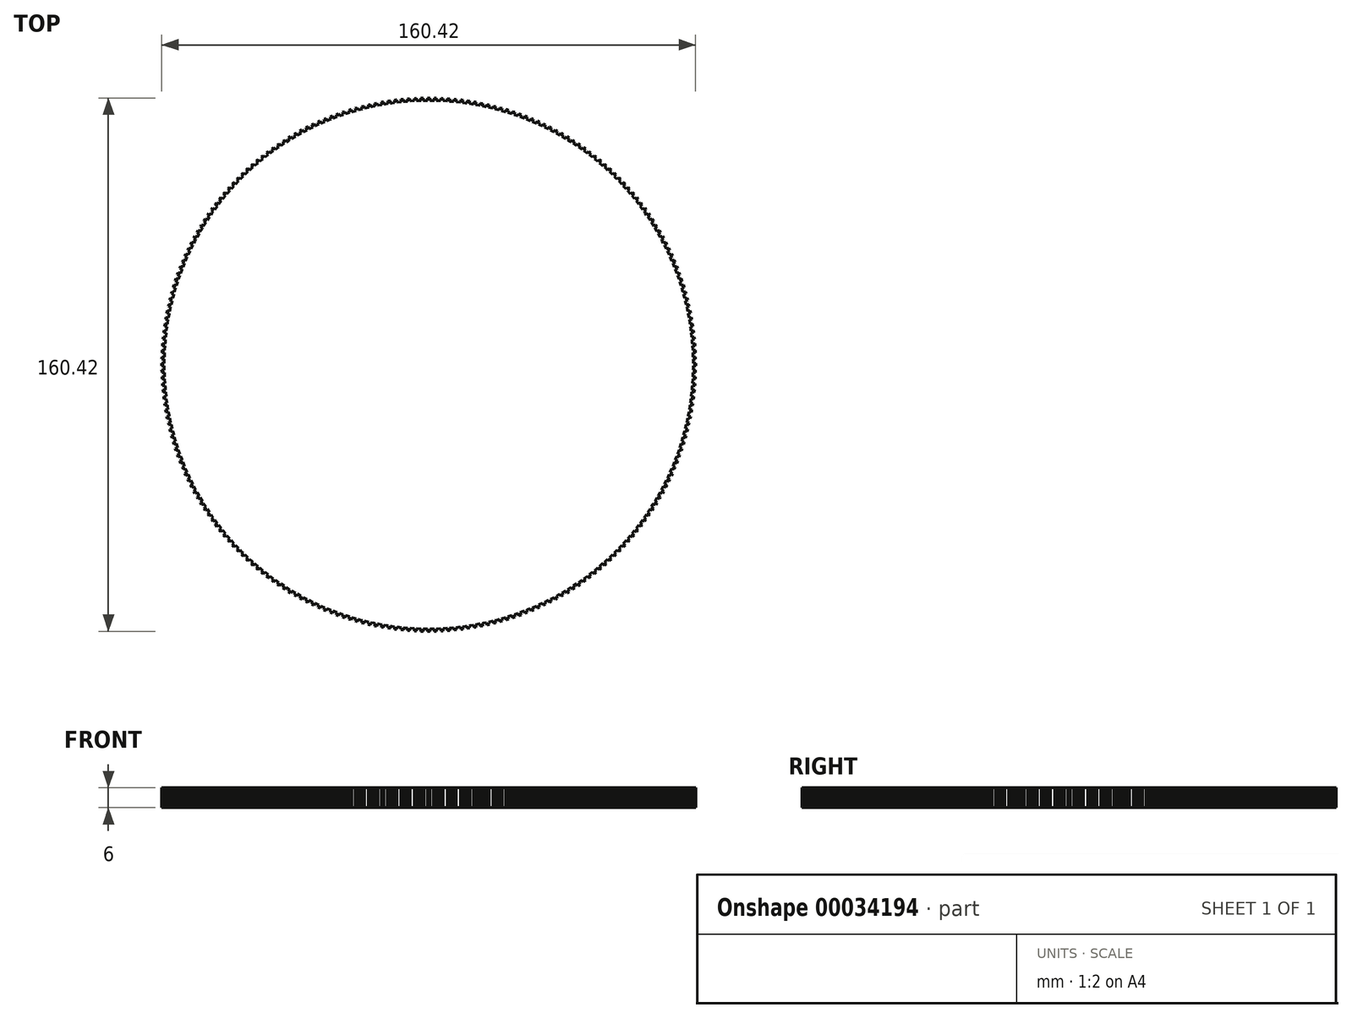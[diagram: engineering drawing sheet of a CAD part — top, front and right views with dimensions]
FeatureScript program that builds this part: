
annotation { "Feature Type Name" : "Feature", "Feature Type Description" : "" }
export const myFeature = defineFeature(function(context is Context, id is Id, definition is map)
    precondition{}
    {
        {
            var Q0;
            Q0=qCreatedBy(makeId("Top.planeOp"),FACE);
            var sketch = newSketch(context, id + "F0", { "sketchPlane" : qUnion([Q0])});
            skLineSegment(sketch, "E0", {"start": v(0.35, -80.21) * mm, "end": v(0.35, -79.46) * mm});
            skLineSegment(sketch, "E1", {"start": v(0.35, -79.46) * mm, "end": v(1.39, -79.45) * mm});
            skLineSegment(sketch, "E2", {"start": v(1.39, -79.45) * mm, "end": v(1.63, -79.45) * mm});
            skLineSegment(sketch, "E3", {"start": v(1.63, -79.45) * mm, "end": v(1.65, -80.2) * mm});
            skLineSegment(sketch, "E4", {"start": v(1.65, -80.2) * mm, "end": v(2.35, -80.18) * mm});
            skLineSegment(sketch, "E5", {"start": v(2.35, -80.18) * mm, "end": v(2.33, -79.43) * mm});
            skLineSegment(sketch, "E6", {"start": v(2.33, -79.43) * mm, "end": v(2.77, -79.42) * mm});
            skLineSegment(sketch, "E7", {"start": v(2.77, -79.42) * mm, "end": v(3.61, -79.38) * mm});
            skLineSegment(sketch, "E8", {"start": v(3.61, -79.38) * mm, "end": v(3.65, -80.13) * mm});
            skLineSegment(sketch, "E9", {"start": v(3.65, -80.13) * mm, "end": v(4.2, -80.1) * mm});
            skLineSegment(sketch, "E10", {"start": v(4.2, -80.1) * mm, "end": v(4.35, -80.1) * mm});
            skLineSegment(sketch, "E11", {"start": v(4.35, -80.1) * mm, "end": v(4.31, -79.35) * mm});
            skLineSegment(sketch, "E12", {"start": v(4.31, -79.35) * mm, "end": v(5.59, -79.27) * mm});
            skLineSegment(sketch, "E13", {"start": v(5.59, -79.27) * mm, "end": v(5.65, -80.01) * mm});
            skLineSegment(sketch, "E14", {"start": v(5.65, -80.01) * mm, "end": v(6.34, -79.96) * mm});
            skLineSegment(sketch, "E15", {"start": v(6.34, -79.96) * mm, "end": v(6.29, -79.21) * mm});
            skLineSegment(sketch, "E16", {"start": v(6.29, -79.21) * mm, "end": v(6.93, -79.16) * mm});
            skLineSegment(sketch, "E17", {"start": v(6.93, -79.16) * mm, "end": v(7.56, -79.1) * mm});
            skLineSegment(sketch, "E18", {"start": v(7.56, -79.1) * mm, "end": v(7.64, -79.85) * mm});
            skLineSegment(sketch, "E19", {"start": v(7.64, -79.85) * mm, "end": v(8.33, -79.78) * mm});
            skLineSegment(sketch, "E20", {"start": v(8.33, -79.78) * mm, "end": v(8.26, -79.03) * mm});
            skLineSegment(sketch, "E21", {"start": v(8.26, -79.03) * mm, "end": v(9.53, -78.89) * mm});
            skLineSegment(sketch, "E22", {"start": v(9.53, -78.89) * mm, "end": v(9.63, -79.63) * mm});
            skLineSegment(sketch, "E23", {"start": v(9.63, -79.63) * mm, "end": v(9.78, -79.62) * mm});
            skLineSegment(sketch, "E24", {"start": v(9.78, -79.62) * mm, "end": v(10.32, -79.54) * mm});
            skLineSegment(sketch, "E25", {"start": v(10.32, -79.54) * mm, "end": v(10.23, -78.8) * mm});
            skLineSegment(sketch, "E26", {"start": v(10.23, -78.8) * mm, "end": v(11.06, -78.7) * mm});
            skLineSegment(sketch, "E27", {"start": v(11.06, -78.7) * mm, "end": v(11.5, -78.63) * mm});
            skLineSegment(sketch, "E28", {"start": v(11.5, -78.63) * mm, "end": v(11.6, -79.37) * mm});
            skLineSegment(sketch, "E29", {"start": v(11.6, -79.37) * mm, "end": v(12.3, -79.26) * mm});
            skLineSegment(sketch, "E30", {"start": v(12.3, -79.26) * mm, "end": v(12.19, -78.52) * mm});
            skLineSegment(sketch, "E31", {"start": v(12.19, -78.52) * mm, "end": v(12.43, -78.49) * mm});
            skLineSegment(sketch, "E32", {"start": v(12.43, -78.49) * mm, "end": v(13.45, -78.31) * mm});
            skLineSegment(sketch, "E33", {"start": v(13.45, -78.31) * mm, "end": v(13.58, -79.05) * mm});
            skLineSegment(sketch, "E34", {"start": v(13.58, -79.05) * mm, "end": v(13.93, -79) * mm});
            skLineSegment(sketch, "E35", {"start": v(13.93, -79) * mm, "end": v(14.27, -78.93) * mm});
            skLineSegment(sketch, "E36", {"start": v(14.27, -78.93) * mm, "end": v(14.14, -78.2) * mm});
            skLineSegment(sketch, "E37", {"start": v(14.14, -78.2) * mm, "end": v(15.16, -78) * mm});
            skLineSegment(sketch, "E38", {"start": v(15.16, -78) * mm, "end": v(15.4, -77.96) * mm});
            skLineSegment(sketch, "E39", {"start": v(15.4, -77.96) * mm, "end": v(15.55, -78.7) * mm});
            skLineSegment(sketch, "E40", {"start": v(15.55, -78.7) * mm, "end": v(16.24, -78.55) * mm});
            skLineSegment(sketch, "E41", {"start": v(16.24, -78.55) * mm, "end": v(16.09, -77.82) * mm});
            skLineSegment(sketch, "E42", {"start": v(16.09, -77.82) * mm, "end": v(16.52, -77.73) * mm});
            skLineSegment(sketch, "E43", {"start": v(16.52, -77.73) * mm, "end": v(17.34, -77.55) * mm});
            skLineSegment(sketch, "E44", {"start": v(17.34, -77.55) * mm, "end": v(17.5, -78.28) * mm});
            skLineSegment(sketch, "E45", {"start": v(17.5, -78.28) * mm, "end": v(18.04, -78.16) * mm});
            skLineSegment(sketch, "E46", {"start": v(18.04, -78.16) * mm, "end": v(18.2, -78.12) * mm});
            skLineSegment(sketch, "E47", {"start": v(18.2, -78.12) * mm, "end": v(18.02, -77.4) * mm});
            skLineSegment(sketch, "E48", {"start": v(18.02, -77.4) * mm, "end": v(19.27, -77.1) * mm});
            skLineSegment(sketch, "E49", {"start": v(19.27, -77.1) * mm, "end": v(19.45, -77.82) * mm});
            skLineSegment(sketch, "E50", {"start": v(19.45, -77.82) * mm, "end": v(20.13, -77.64) * mm});
            skLineSegment(sketch, "E51", {"start": v(20.13, -77.64) * mm, "end": v(19.95, -76.92) * mm});
            skLineSegment(sketch, "E52", {"start": v(19.95, -76.92) * mm, "end": v(20.57, -76.76) * mm});
            skLineSegment(sketch, "E53", {"start": v(20.57, -76.76) * mm, "end": v(21.18, -76.59) * mm});
            skLineSegment(sketch, "E54", {"start": v(21.18, -76.59) * mm, "end": v(21.39, -77.3) * mm});
            skLineSegment(sketch, "E55", {"start": v(21.39, -77.3) * mm, "end": v(22.06, -77.12) * mm});
            skLineSegment(sketch, "E56", {"start": v(22.06, -77.12) * mm, "end": v(21.86, -76.4) * mm});
            skLineSegment(sketch, "E57", {"start": v(21.86, -76.4) * mm, "end": v(23.09, -76.03) * mm});
            skLineSegment(sketch, "E58", {"start": v(23.09, -76.03) * mm, "end": v(23.3, -76.75) * mm});
            skLineSegment(sketch, "E59", {"start": v(23.3, -76.75) * mm, "end": v(23.45, -76.7) * mm});
            skLineSegment(sketch, "E60", {"start": v(23.45, -76.7) * mm, "end": v(23.98, -76.54) * mm});
            skLineSegment(sketch, "E61", {"start": v(23.98, -76.54) * mm, "end": v(23.76, -75.83) * mm});
            skLineSegment(sketch, "E62", {"start": v(23.76, -75.83) * mm, "end": v(24.56, -75.57) * mm});
            skLineSegment(sketch, "E63", {"start": v(24.56, -75.57) * mm, "end": v(24.98, -75.43) * mm});
            skLineSegment(sketch, "E64", {"start": v(24.98, -75.43) * mm, "end": v(25.21, -76.15) * mm});
            skLineSegment(sketch, "E65", {"start": v(25.21, -76.15) * mm, "end": v(25.88, -75.92) * mm});
            skLineSegment(sketch, "E66", {"start": v(25.88, -75.92) * mm, "end": v(25.64, -75.21) * mm});
            skLineSegment(sketch, "E67", {"start": v(25.64, -75.21) * mm, "end": v(25.87, -75.13) * mm});
            skLineSegment(sketch, "E68", {"start": v(25.87, -75.13) * mm, "end": v(26.85, -74.79) * mm});
            skLineSegment(sketch, "E69", {"start": v(26.85, -74.79) * mm, "end": v(27.1, -75.5) * mm});
            skLineSegment(sketch, "E70", {"start": v(27.1, -75.5) * mm, "end": v(27.43, -75.38) * mm});
            skLineSegment(sketch, "E71", {"start": v(27.43, -75.38) * mm, "end": v(27.76, -75.25) * mm});
            skLineSegment(sketch, "E72", {"start": v(27.76, -75.25) * mm, "end": v(27.5, -74.55) * mm});
            skLineSegment(sketch, "E73", {"start": v(27.5, -74.55) * mm, "end": v(28.48, -74.19) * mm});
            skLineSegment(sketch, "E74", {"start": v(28.48, -74.19) * mm, "end": v(28.7, -74.1) * mm});
            skLineSegment(sketch, "E75", {"start": v(28.7, -74.1) * mm, "end": v(28.98, -74.8) * mm});
            skLineSegment(sketch, "E76", {"start": v(28.98, -74.8) * mm, "end": v(29.63, -74.54) * mm});
            skLineSegment(sketch, "E77", {"start": v(29.63, -74.54) * mm, "end": v(29.36, -73.84) * mm});
            skLineSegment(sketch, "E78", {"start": v(29.36, -73.84) * mm, "end": v(29.77, -73.68) * mm});
            skLineSegment(sketch, "E79", {"start": v(29.77, -73.68) * mm, "end": v(30.54, -73.36) * mm});
            skLineSegment(sketch, "E80", {"start": v(30.54, -73.36) * mm, "end": v(30.83, -74.05) * mm});
            skLineSegment(sketch, "E81", {"start": v(30.83, -74.05) * mm, "end": v(31.34, -73.84) * mm});
            skLineSegment(sketch, "E82", {"start": v(31.34, -73.84) * mm, "end": v(31.48, -73.78) * mm});
            skLineSegment(sketch, "E83", {"start": v(31.48, -73.78) * mm, "end": v(31.19, -73.09) * mm});
            skLineSegment(sketch, "E84", {"start": v(31.19, -73.09) * mm, "end": v(32.36, -72.57) * mm});
            skLineSegment(sketch, "E85", {"start": v(32.36, -72.57) * mm, "end": v(32.67, -73.26) * mm});
            skLineSegment(sketch, "E86", {"start": v(32.67, -73.26) * mm, "end": v(33.3, -72.97) * mm});
            skLineSegment(sketch, "E87", {"start": v(33.3, -72.97) * mm, "end": v(33, -72.28) * mm});
            skLineSegment(sketch, "E88", {"start": v(33, -72.28) * mm, "end": v(33.58, -72.02) * mm});
            skLineSegment(sketch, "E89", {"start": v(33.58, -72.02) * mm, "end": v(34.16, -71.74) * mm});
            skLineSegment(sketch, "E90", {"start": v(34.16, -71.74) * mm, "end": v(34.49, -72.42) * mm});
            skLineSegment(sketch, "E91", {"start": v(34.49, -72.42) * mm, "end": v(35.12, -72.12) * mm});
            skLineSegment(sketch, "E92", {"start": v(35.12, -72.12) * mm, "end": v(34.8, -71.44) * mm});
            skLineSegment(sketch, "E93", {"start": v(34.8, -71.44) * mm, "end": v(35.94, -70.87) * mm});
            skLineSegment(sketch, "E94", {"start": v(35.94, -70.87) * mm, "end": v(36.28, -71.54) * mm});
            skLineSegment(sketch, "E95", {"start": v(36.28, -71.54) * mm, "end": v(36.42, -71.47) * mm});
            skLineSegment(sketch, "E96", {"start": v(36.42, -71.47) * mm, "end": v(36.9, -71.22) * mm});
            skLineSegment(sketch, "E97", {"start": v(36.9, -71.22) * mm, "end": v(36.56, -70.55) * mm});
            skLineSegment(sketch, "E98", {"start": v(36.56, -70.55) * mm, "end": v(37.3, -70.16) * mm});
            skLineSegment(sketch, "E99", {"start": v(37.3, -70.16) * mm, "end": v(37.7, -69.95) * mm});
            skLineSegment(sketch, "E100", {"start": v(37.7, -69.95) * mm, "end": v(38.05, -70.61) * mm});
            skLineSegment(sketch, "E101", {"start": v(38.05, -70.61) * mm, "end": v(38.67, -70.28) * mm});
            skLineSegment(sketch, "E102", {"start": v(38.67, -70.28) * mm, "end": v(38.31, -69.62) * mm});
            skLineSegment(sketch, "E103", {"start": v(38.31, -69.62) * mm, "end": v(38.52, -69.5) * mm});
            skLineSegment(sketch, "E104", {"start": v(38.52, -69.5) * mm, "end": v(39.43, -69) * mm});
            skLineSegment(sketch, "E105", {"start": v(39.43, -69) * mm, "end": v(39.8, -69.64) * mm});
            skLineSegment(sketch, "E106", {"start": v(39.8, -69.64) * mm, "end": v(40.1, -69.47) * mm});
            skLineSegment(sketch, "E107", {"start": v(40.1, -69.47) * mm, "end": v(40.4, -69.29) * mm});
            skLineSegment(sketch, "E108", {"start": v(40.4, -69.29) * mm, "end": v(40.03, -68.64) * mm});
            skLineSegment(sketch, "E109", {"start": v(40.03, -68.64) * mm, "end": v(40.93, -68.11) * mm});
            skLineSegment(sketch, "E110", {"start": v(40.93, -68.11) * mm, "end": v(41.14, -67.99) * mm});
            skLineSegment(sketch, "E111", {"start": v(41.14, -67.99) * mm, "end": v(41.53, -68.63) * mm});
            skLineSegment(sketch, "E112", {"start": v(41.53, -68.63) * mm, "end": v(42.12, -68.26) * mm});
            skLineSegment(sketch, "E113", {"start": v(42.12, -68.26) * mm, "end": v(41.73, -67.62) * mm});
            skLineSegment(sketch, "E114", {"start": v(41.73, -67.62) * mm, "end": v(42.1, -67.39) * mm});
            skLineSegment(sketch, "E115", {"start": v(42.1, -67.39) * mm, "end": v(42.82, -66.94) * mm});
            skLineSegment(sketch, "E116", {"start": v(42.82, -66.94) * mm, "end": v(43.22, -67.57) * mm});
            skLineSegment(sketch, "E117", {"start": v(43.22, -67.57) * mm, "end": v(43.69, -67.27) * mm});
            skLineSegment(sketch, "E118", {"start": v(43.69, -67.27) * mm, "end": v(43.81, -67.2) * mm});
            skLineSegment(sketch, "E119", {"start": v(43.81, -67.2) * mm, "end": v(43.4, -66.56) * mm});
            skLineSegment(sketch, "E120", {"start": v(43.4, -66.56) * mm, "end": v(44.47, -65.85) * mm});
            skLineSegment(sketch, "E121", {"start": v(44.47, -65.85) * mm, "end": v(44.9, -66.47) * mm});
            skLineSegment(sketch, "E122", {"start": v(44.9, -66.47) * mm, "end": v(45.47, -66.08) * mm});
            skLineSegment(sketch, "E123", {"start": v(45.47, -66.08) * mm, "end": v(45.05, -65.46) * mm});
            skLineSegment(sketch, "E124", {"start": v(45.05, -65.46) * mm, "end": v(45.58, -65.1) * mm});
            skLineSegment(sketch, "E125", {"start": v(45.58, -65.1) * mm, "end": v(46.1, -64.72) * mm});
            skLineSegment(sketch, "E126", {"start": v(46.1, -64.72) * mm, "end": v(46.54, -65.33) * mm});
            skLineSegment(sketch, "E127", {"start": v(46.54, -65.33) * mm, "end": v(47.1, -64.92) * mm});
            skLineSegment(sketch, "E128", {"start": v(47.1, -64.92) * mm, "end": v(46.67, -64.31) * mm});
            skLineSegment(sketch, "E129", {"start": v(46.67, -64.31) * mm, "end": v(47.7, -63.55) * mm});
            skLineSegment(sketch, "E130", {"start": v(47.7, -63.55) * mm, "end": v(48.15, -64.15) * mm});
            skLineSegment(sketch, "E131", {"start": v(48.15, -64.15) * mm, "end": v(48.27, -64.06) * mm});
            skLineSegment(sketch, "E132", {"start": v(48.27, -64.06) * mm, "end": v(48.71, -63.73) * mm});
            skLineSegment(sketch, "E133", {"start": v(48.71, -63.73) * mm, "end": v(48.26, -63.13) * mm});
            skLineSegment(sketch, "E134", {"start": v(48.26, -63.13) * mm, "end": v(48.92, -62.62) * mm});
            skLineSegment(sketch, "E135", {"start": v(48.92, -62.62) * mm, "end": v(49.27, -62.34) * mm});
            skLineSegment(sketch, "E136", {"start": v(49.27, -62.34) * mm, "end": v(49.74, -62.93) * mm});
            skLineSegment(sketch, "E137", {"start": v(49.74, -62.93) * mm, "end": v(50.28, -62.5) * mm});
            skLineSegment(sketch, "E138", {"start": v(50.28, -62.5) * mm, "end": v(49.82, -61.9) * mm});
            skLineSegment(sketch, "E139", {"start": v(49.82, -61.9) * mm, "end": v(50, -61.76) * mm});
            skLineSegment(sketch, "E140", {"start": v(50, -61.76) * mm, "end": v(50.8, -61.1) * mm});
            skLineSegment(sketch, "E141", {"start": v(50.8, -61.1) * mm, "end": v(51.3, -61.67) * mm});
            skLineSegment(sketch, "E142", {"start": v(51.3, -61.67) * mm, "end": v(51.56, -61.45) * mm});
            skLineSegment(sketch, "E143", {"start": v(51.56, -61.45) * mm, "end": v(51.83, -61.22) * mm});
            skLineSegment(sketch, "E144", {"start": v(51.83, -61.22) * mm, "end": v(51.34, -60.65) * mm});
            skLineSegment(sketch, "E145", {"start": v(51.34, -60.65) * mm, "end": v(52.13, -59.97) * mm});
            skLineSegment(sketch, "E146", {"start": v(52.13, -59.97) * mm, "end": v(52.32, -59.81) * mm});
            skLineSegment(sketch, "E147", {"start": v(52.32, -59.81) * mm, "end": v(52.81, -60.37) * mm});
            skLineSegment(sketch, "E148", {"start": v(52.81, -60.37) * mm, "end": v(53.34, -59.9) * mm});
            skLineSegment(sketch, "E149", {"start": v(53.34, -59.9) * mm, "end": v(52.84, -59.35) * mm});
            skLineSegment(sketch, "E150", {"start": v(52.84, -59.35) * mm, "end": v(53.17, -59.05) * mm});
            skLineSegment(sketch, "E151", {"start": v(53.17, -59.05) * mm, "end": v(53.8, -58.49) * mm});
            skLineSegment(sketch, "E152", {"start": v(53.8, -58.49) * mm, "end": v(54.3, -59.04) * mm});
            skLineSegment(sketch, "E153", {"start": v(54.3, -59.04) * mm, "end": v(54.7, -58.66) * mm});
            skLineSegment(sketch, "E154", {"start": v(54.7, -58.66) * mm, "end": v(54.81, -58.56) * mm});
            skLineSegment(sketch, "E155", {"start": v(54.81, -58.56) * mm, "end": v(54.3, -58.01) * mm});
            skLineSegment(sketch, "E156", {"start": v(54.3, -58.01) * mm, "end": v(55.23, -57.13) * mm});
            skLineSegment(sketch, "E157", {"start": v(55.23, -57.13) * mm, "end": v(55.76, -57.67) * mm});
            skLineSegment(sketch, "E158", {"start": v(55.76, -57.67) * mm, "end": v(56.26, -57.18) * mm});
            skLineSegment(sketch, "E159", {"start": v(56.26, -57.18) * mm, "end": v(55.73, -56.64) * mm});
            skLineSegment(sketch, "E160", {"start": v(55.73, -56.64) * mm, "end": v(56.19, -56.19) * mm});
            skLineSegment(sketch, "E161", {"start": v(56.19, -56.19) * mm, "end": v(56.64, -55.73) * mm});
            skLineSegment(sketch, "E162", {"start": v(56.64, -55.73) * mm, "end": v(57.18, -56.26) * mm});
            skLineSegment(sketch, "E163", {"start": v(57.18, -56.26) * mm, "end": v(57.67, -55.76) * mm});
            skLineSegment(sketch, "E164", {"start": v(57.67, -55.76) * mm, "end": v(57.13, -55.23) * mm});
            skLineSegment(sketch, "E165", {"start": v(57.13, -55.23) * mm, "end": v(58.01, -54.3) * mm});
            skLineSegment(sketch, "E166", {"start": v(58.01, -54.3) * mm, "end": v(58.56, -54.81) * mm});
            skLineSegment(sketch, "E167", {"start": v(58.56, -54.81) * mm, "end": v(58.66, -54.7) * mm});
            skLineSegment(sketch, "E168", {"start": v(58.66, -54.7) * mm, "end": v(59.04, -54.3) * mm});
            skLineSegment(sketch, "E169", {"start": v(59.04, -54.3) * mm, "end": v(58.49, -53.8) * mm});
            skLineSegment(sketch, "E170", {"start": v(58.49, -53.8) * mm, "end": v(59.05, -53.17) * mm});
            skLineSegment(sketch, "E171", {"start": v(59.05, -53.17) * mm, "end": v(59.35, -52.84) * mm});
            skLineSegment(sketch, "E172", {"start": v(59.35, -52.84) * mm, "end": v(59.9, -53.34) * mm});
            skLineSegment(sketch, "E173", {"start": v(59.9, -53.34) * mm, "end": v(60.37, -52.81) * mm});
            skLineSegment(sketch, "E174", {"start": v(60.37, -52.81) * mm, "end": v(59.81, -52.32) * mm});
            skLineSegment(sketch, "E175", {"start": v(59.81, -52.32) * mm, "end": v(59.97, -52.13) * mm});
            skLineSegment(sketch, "E176", {"start": v(59.97, -52.13) * mm, "end": v(60.65, -51.34) * mm});
            skLineSegment(sketch, "E177", {"start": v(60.65, -51.34) * mm, "end": v(61.22, -51.83) * mm});
            skLineSegment(sketch, "E178", {"start": v(61.22, -51.83) * mm, "end": v(61.45, -51.56) * mm});
            skLineSegment(sketch, "E179", {"start": v(61.45, -51.56) * mm, "end": v(61.67, -51.3) * mm});
            skLineSegment(sketch, "E180", {"start": v(61.67, -51.3) * mm, "end": v(61.1, -50.8) * mm});
            skLineSegment(sketch, "E181", {"start": v(61.1, -50.8) * mm, "end": v(61.76, -50) * mm});
            skLineSegment(sketch, "E182", {"start": v(61.76, -50) * mm, "end": v(61.9, -49.82) * mm});
            skLineSegment(sketch, "E183", {"start": v(61.9, -49.82) * mm, "end": v(62.5, -50.28) * mm});
            skLineSegment(sketch, "E184", {"start": v(62.5, -50.28) * mm, "end": v(62.93, -49.74) * mm});
            skLineSegment(sketch, "E185", {"start": v(62.93, -49.74) * mm, "end": v(62.34, -49.27) * mm});
            skLineSegment(sketch, "E186", {"start": v(62.34, -49.27) * mm, "end": v(62.62, -48.92) * mm});
            skLineSegment(sketch, "E187", {"start": v(62.62, -48.92) * mm, "end": v(63.13, -48.26) * mm});
            skLineSegment(sketch, "E188", {"start": v(63.13, -48.26) * mm, "end": v(63.73, -48.71) * mm});
            skLineSegment(sketch, "E189", {"start": v(63.73, -48.71) * mm, "end": v(64.06, -48.27) * mm});
            skLineSegment(sketch, "E190", {"start": v(64.06, -48.27) * mm, "end": v(64.15, -48.15) * mm});
            skLineSegment(sketch, "E191", {"start": v(64.15, -48.15) * mm, "end": v(63.55, -47.7) * mm});
            skLineSegment(sketch, "E192", {"start": v(63.55, -47.7) * mm, "end": v(64.31, -46.67) * mm});
            skLineSegment(sketch, "E193", {"start": v(64.31, -46.67) * mm, "end": v(64.92, -47.1) * mm});
            skLineSegment(sketch, "E194", {"start": v(64.92, -47.1) * mm, "end": v(65.33, -46.54) * mm});
            skLineSegment(sketch, "E195", {"start": v(65.33, -46.54) * mm, "end": v(64.72, -46.1) * mm});
            skLineSegment(sketch, "E196", {"start": v(64.72, -46.1) * mm, "end": v(65.1, -45.58) * mm});
            skLineSegment(sketch, "E197", {"start": v(65.1, -45.58) * mm, "end": v(65.46, -45.05) * mm});
            skLineSegment(sketch, "E198", {"start": v(65.46, -45.05) * mm, "end": v(66.08, -45.47) * mm});
            skLineSegment(sketch, "E199", {"start": v(66.08, -45.47) * mm, "end": v(66.47, -44.9) * mm});
            skLineSegment(sketch, "E200", {"start": v(66.47, -44.9) * mm, "end": v(65.85, -44.47) * mm});
            skLineSegment(sketch, "E201", {"start": v(65.85, -44.47) * mm, "end": v(66.56, -43.4) * mm});
            skLineSegment(sketch, "E202", {"start": v(66.56, -43.4) * mm, "end": v(67.2, -43.81) * mm});
            skLineSegment(sketch, "E203", {"start": v(67.2, -43.81) * mm, "end": v(67.27, -43.69) * mm});
            skLineSegment(sketch, "E204", {"start": v(67.27, -43.69) * mm, "end": v(67.57, -43.22) * mm});
            skLineSegment(sketch, "E205", {"start": v(67.57, -43.22) * mm, "end": v(66.94, -42.82) * mm});
            skLineSegment(sketch, "E206", {"start": v(66.94, -42.82) * mm, "end": v(67.39, -42.1) * mm});
            skLineSegment(sketch, "E207", {"start": v(67.39, -42.1) * mm, "end": v(67.62, -41.73) * mm});
            skLineSegment(sketch, "E208", {"start": v(67.62, -41.73) * mm, "end": v(68.26, -42.12) * mm});
            skLineSegment(sketch, "E209", {"start": v(68.26, -42.12) * mm, "end": v(68.63, -41.53) * mm});
            skLineSegment(sketch, "E210", {"start": v(68.63, -41.53) * mm, "end": v(67.99, -41.14) * mm});
            skLineSegment(sketch, "E211", {"start": v(67.99, -41.14) * mm, "end": v(68.11, -40.93) * mm});
            skLineSegment(sketch, "E212", {"start": v(68.11, -40.93) * mm, "end": v(68.64, -40.03) * mm});
            skLineSegment(sketch, "E213", {"start": v(68.64, -40.03) * mm, "end": v(69.29, -40.4) * mm});
            skLineSegment(sketch, "E214", {"start": v(69.29, -40.4) * mm, "end": v(69.47, -40.1) * mm});
            skLineSegment(sketch, "E215", {"start": v(69.47, -40.1) * mm, "end": v(69.64, -39.8) * mm});
            skLineSegment(sketch, "E216", {"start": v(69.64, -39.8) * mm, "end": v(69, -39.43) * mm});
            skLineSegment(sketch, "E217", {"start": v(69, -39.43) * mm, "end": v(69.5, -38.52) * mm});
            skLineSegment(sketch, "E218", {"start": v(69.5, -38.52) * mm, "end": v(69.62, -38.31) * mm});
            skLineSegment(sketch, "E219", {"start": v(69.62, -38.31) * mm, "end": v(70.28, -38.67) * mm});
            skLineSegment(sketch, "E220", {"start": v(70.28, -38.67) * mm, "end": v(70.61, -38.05) * mm});
            skLineSegment(sketch, "E221", {"start": v(70.61, -38.05) * mm, "end": v(69.95, -37.7) * mm});
            skLineSegment(sketch, "E222", {"start": v(69.95, -37.7) * mm, "end": v(70.16, -37.3) * mm});
            skLineSegment(sketch, "E223", {"start": v(70.16, -37.3) * mm, "end": v(70.55, -36.56) * mm});
            skLineSegment(sketch, "E224", {"start": v(70.55, -36.56) * mm, "end": v(71.22, -36.9) * mm});
            skLineSegment(sketch, "E225", {"start": v(71.22, -36.9) * mm, "end": v(71.47, -36.42) * mm});
            skLineSegment(sketch, "E226", {"start": v(71.47, -36.42) * mm, "end": v(71.54, -36.28) * mm});
            skLineSegment(sketch, "E227", {"start": v(71.54, -36.28) * mm, "end": v(70.87, -35.94) * mm});
            skLineSegment(sketch, "E228", {"start": v(70.87, -35.94) * mm, "end": v(71.44, -34.8) * mm});
            skLineSegment(sketch, "E229", {"start": v(71.44, -34.8) * mm, "end": v(72.12, -35.12) * mm});
            skLineSegment(sketch, "E230", {"start": v(72.12, -35.12) * mm, "end": v(72.42, -34.49) * mm});
            skLineSegment(sketch, "E231", {"start": v(72.42, -34.49) * mm, "end": v(71.74, -34.16) * mm});
            skLineSegment(sketch, "E232", {"start": v(71.74, -34.16) * mm, "end": v(72.02, -33.58) * mm});
            skLineSegment(sketch, "E233", {"start": v(72.02, -33.58) * mm, "end": v(72.28, -33) * mm});
            skLineSegment(sketch, "E234", {"start": v(72.28, -33) * mm, "end": v(72.97, -33.3) * mm});
            skLineSegment(sketch, "E235", {"start": v(72.97, -33.3) * mm, "end": v(73.26, -32.67) * mm});
            skLineSegment(sketch, "E236", {"start": v(73.26, -32.67) * mm, "end": v(72.57, -32.36) * mm});
            skLineSegment(sketch, "E237", {"start": v(72.57, -32.36) * mm, "end": v(73.09, -31.19) * mm});
            skLineSegment(sketch, "E238", {"start": v(73.09, -31.19) * mm, "end": v(73.78, -31.48) * mm});
            skLineSegment(sketch, "E239", {"start": v(73.78, -31.48) * mm, "end": v(73.84, -31.34) * mm});
            skLineSegment(sketch, "E240", {"start": v(73.84, -31.34) * mm, "end": v(74.05, -30.83) * mm});
            skLineSegment(sketch, "E241", {"start": v(74.05, -30.83) * mm, "end": v(73.36, -30.54) * mm});
            skLineSegment(sketch, "E242", {"start": v(73.36, -30.54) * mm, "end": v(73.68, -29.77) * mm});
            skLineSegment(sketch, "E243", {"start": v(73.68, -29.77) * mm, "end": v(73.84, -29.36) * mm});
            skLineSegment(sketch, "E244", {"start": v(73.84, -29.36) * mm, "end": v(74.54, -29.63) * mm});
            skLineSegment(sketch, "E245", {"start": v(74.54, -29.63) * mm, "end": v(74.8, -28.98) * mm});
            skLineSegment(sketch, "E246", {"start": v(74.8, -28.98) * mm, "end": v(74.1, -28.7) * mm});
            skLineSegment(sketch, "E247", {"start": v(74.1, -28.7) * mm, "end": v(74.19, -28.48) * mm});
            skLineSegment(sketch, "E248", {"start": v(74.19, -28.48) * mm, "end": v(74.55, -27.5) * mm});
            skLineSegment(sketch, "E249", {"start": v(74.55, -27.5) * mm, "end": v(75.25, -27.76) * mm});
            skLineSegment(sketch, "E250", {"start": v(75.25, -27.76) * mm, "end": v(75.38, -27.43) * mm});
            skLineSegment(sketch, "E251", {"start": v(75.38, -27.43) * mm, "end": v(75.5, -27.1) * mm});
            skLineSegment(sketch, "E252", {"start": v(75.5, -27.1) * mm, "end": v(74.79, -26.85) * mm});
            skLineSegment(sketch, "E253", {"start": v(74.79, -26.85) * mm, "end": v(75.13, -25.87) * mm});
            skLineSegment(sketch, "E254", {"start": v(75.13, -25.87) * mm, "end": v(75.21, -25.64) * mm});
            skLineSegment(sketch, "E255", {"start": v(75.21, -25.64) * mm, "end": v(75.92, -25.88) * mm});
            skLineSegment(sketch, "E256", {"start": v(75.92, -25.88) * mm, "end": v(76.15, -25.21) * mm});
            skLineSegment(sketch, "E257", {"start": v(76.15, -25.21) * mm, "end": v(75.43, -24.98) * mm});
            skLineSegment(sketch, "E258", {"start": v(75.43, -24.98) * mm, "end": v(75.57, -24.56) * mm});
            skLineSegment(sketch, "E259", {"start": v(75.57, -24.56) * mm, "end": v(75.83, -23.76) * mm});
            skLineSegment(sketch, "E260", {"start": v(75.83, -23.76) * mm, "end": v(76.54, -23.98) * mm});
            skLineSegment(sketch, "E261", {"start": v(76.54, -23.98) * mm, "end": v(76.7, -23.45) * mm});
            skLineSegment(sketch, "E262", {"start": v(76.7, -23.45) * mm, "end": v(76.75, -23.3) * mm});
            skLineSegment(sketch, "E263", {"start": v(76.75, -23.3) * mm, "end": v(76.03, -23.09) * mm});
            skLineSegment(sketch, "E264", {"start": v(76.03, -23.09) * mm, "end": v(76.4, -21.86) * mm});
            skLineSegment(sketch, "E265", {"start": v(76.4, -21.86) * mm, "end": v(77.12, -22.06) * mm});
            skLineSegment(sketch, "E266", {"start": v(77.12, -22.06) * mm, "end": v(77.3, -21.39) * mm});
            skLineSegment(sketch, "E267", {"start": v(77.3, -21.39) * mm, "end": v(76.59, -21.18) * mm});
            skLineSegment(sketch, "E268", {"start": v(76.59, -21.18) * mm, "end": v(76.76, -20.57) * mm});
            skLineSegment(sketch, "E269", {"start": v(76.76, -20.57) * mm, "end": v(76.92, -19.95) * mm});
            skLineSegment(sketch, "E270", {"start": v(76.92, -19.95) * mm, "end": v(77.64, -20.13) * mm});
            skLineSegment(sketch, "E271", {"start": v(77.64, -20.13) * mm, "end": v(77.82, -19.45) * mm});
            skLineSegment(sketch, "E272", {"start": v(77.82, -19.45) * mm, "end": v(77.1, -19.27) * mm});
            skLineSegment(sketch, "E273", {"start": v(77.1, -19.27) * mm, "end": v(77.4, -18.02) * mm});
            skLineSegment(sketch, "E274", {"start": v(77.4, -18.02) * mm, "end": v(78.12, -18.2) * mm});
            skLineSegment(sketch, "E275", {"start": v(78.12, -18.2) * mm, "end": v(78.16, -18.04) * mm});
            skLineSegment(sketch, "E276", {"start": v(78.16, -18.04) * mm, "end": v(78.28, -17.5) * mm});
            skLineSegment(sketch, "E277", {"start": v(78.28, -17.5) * mm, "end": v(77.55, -17.34) * mm});
            skLineSegment(sketch, "E278", {"start": v(77.55, -17.34) * mm, "end": v(77.73, -16.52) * mm});
            skLineSegment(sketch, "E279", {"start": v(77.73, -16.52) * mm, "end": v(77.82, -16.09) * mm});
            skLineSegment(sketch, "E280", {"start": v(77.82, -16.09) * mm, "end": v(78.55, -16.24) * mm});
            skLineSegment(sketch, "E281", {"start": v(78.55, -16.24) * mm, "end": v(78.7, -15.55) * mm});
            skLineSegment(sketch, "E282", {"start": v(78.7, -15.55) * mm, "end": v(77.96, -15.4) * mm});
            skLineSegment(sketch, "E283", {"start": v(77.96, -15.4) * mm, "end": v(78, -15.16) * mm});
            skLineSegment(sketch, "E284", {"start": v(78, -15.16) * mm, "end": v(78.2, -14.14) * mm});
            skLineSegment(sketch, "E285", {"start": v(78.2, -14.14) * mm, "end": v(78.93, -14.27) * mm});
            skLineSegment(sketch, "E286", {"start": v(78.93, -14.27) * mm, "end": v(79, -13.93) * mm});
            skLineSegment(sketch, "E287", {"start": v(79, -13.93) * mm, "end": v(79.05, -13.58) * mm});
            skLineSegment(sketch, "E288", {"start": v(79.05, -13.58) * mm, "end": v(78.31, -13.45) * mm});
            skLineSegment(sketch, "E289", {"start": v(78.31, -13.45) * mm, "end": v(78.49, -12.43) * mm});
            skLineSegment(sketch, "E290", {"start": v(78.49, -12.43) * mm, "end": v(78.52, -12.19) * mm});
            skLineSegment(sketch, "E291", {"start": v(78.52, -12.19) * mm, "end": v(79.26, -12.3) * mm});
            skLineSegment(sketch, "E292", {"start": v(79.26, -12.3) * mm, "end": v(79.37, -11.6) * mm});
            skLineSegment(sketch, "E293", {"start": v(79.37, -11.6) * mm, "end": v(78.63, -11.5) * mm});
            skLineSegment(sketch, "E294", {"start": v(78.63, -11.5) * mm, "end": v(78.7, -11.06) * mm});
            skLineSegment(sketch, "E295", {"start": v(78.7, -11.06) * mm, "end": v(78.8, -10.23) * mm});
            skLineSegment(sketch, "E296", {"start": v(78.8, -10.23) * mm, "end": v(79.54, -10.32) * mm});
            skLineSegment(sketch, "E297", {"start": v(79.54, -10.32) * mm, "end": v(79.62, -9.78) * mm});
            skLineSegment(sketch, "E298", {"start": v(79.62, -9.78) * mm, "end": v(79.63, -9.63) * mm});
            skLineSegment(sketch, "E299", {"start": v(79.63, -9.63) * mm, "end": v(78.89, -9.53) * mm});
            skLineSegment(sketch, "E300", {"start": v(78.89, -9.53) * mm, "end": v(79.03, -8.26) * mm});
            skLineSegment(sketch, "E301", {"start": v(79.03, -8.26) * mm, "end": v(79.78, -8.33) * mm});
            skLineSegment(sketch, "E302", {"start": v(79.78, -8.33) * mm, "end": v(79.85, -7.64) * mm});
            skLineSegment(sketch, "E303", {"start": v(79.85, -7.64) * mm, "end": v(79.1, -7.56) * mm});
            skLineSegment(sketch, "E304", {"start": v(79.1, -7.56) * mm, "end": v(79.16, -6.93) * mm});
            skLineSegment(sketch, "E305", {"start": v(79.16, -6.93) * mm, "end": v(79.21, -6.29) * mm});
            skLineSegment(sketch, "E306", {"start": v(79.21, -6.29) * mm, "end": v(79.96, -6.34) * mm});
            skLineSegment(sketch, "E307", {"start": v(79.96, -6.34) * mm, "end": v(80.01, -5.65) * mm});
            skLineSegment(sketch, "E308", {"start": v(80.01, -5.65) * mm, "end": v(79.27, -5.59) * mm});
            skLineSegment(sketch, "E309", {"start": v(79.27, -5.59) * mm, "end": v(79.35, -4.31) * mm});
            skLineSegment(sketch, "E310", {"start": v(79.35, -4.31) * mm, "end": v(80.1, -4.35) * mm});
            skLineSegment(sketch, "E311", {"start": v(80.1, -4.35) * mm, "end": v(80.1, -4.2) * mm});
            skLineSegment(sketch, "E312", {"start": v(80.1, -4.2) * mm, "end": v(80.13, -3.65) * mm});
            skLineSegment(sketch, "E313", {"start": v(80.13, -3.65) * mm, "end": v(79.38, -3.61) * mm});
            skLineSegment(sketch, "E314", {"start": v(79.38, -3.61) * mm, "end": v(79.42, -2.77) * mm});
            skLineSegment(sketch, "E315", {"start": v(79.42, -2.77) * mm, "end": v(79.43, -2.33) * mm});
            skLineSegment(sketch, "E316", {"start": v(79.43, -2.33) * mm, "end": v(80.18, -2.35) * mm});
            skLineSegment(sketch, "E317", {"start": v(80.18, -2.35) * mm, "end": v(80.2, -1.65) * mm});
            skLineSegment(sketch, "E318", {"start": v(80.2, -1.65) * mm, "end": v(79.45, -1.63) * mm});
            skLineSegment(sketch, "E319", {"start": v(79.45, -1.63) * mm, "end": v(79.45, -1.39) * mm});
            skLineSegment(sketch, "E320", {"start": v(79.45, -1.39) * mm, "end": v(79.46, -0.35) * mm});
            skLineSegment(sketch, "E321", {"start": v(79.46, -0.35) * mm, "end": v(80.21, -0.35) * mm});
            skLineSegment(sketch, "E322", {"start": v(80.21, -0.35) * mm, "end": v(80.21, 0) * mm});
            skLineSegment(sketch, "E323", {"start": v(80.21, 0) * mm, "end": v(80.21, 0.35) * mm});
            skLineSegment(sketch, "E324", {"start": v(80.21, 0.35) * mm, "end": v(79.46, 0.35) * mm});
            skLineSegment(sketch, "E325", {"start": v(79.46, 0.35) * mm, "end": v(79.45, 1.39) * mm});
            skLineSegment(sketch, "E326", {"start": v(79.45, 1.39) * mm, "end": v(79.45, 1.63) * mm});
            skLineSegment(sketch, "E327", {"start": v(79.45, 1.63) * mm, "end": v(80.2, 1.65) * mm});
            skLineSegment(sketch, "E328", {"start": v(80.2, 1.65) * mm, "end": v(80.18, 2.35) * mm});
            skLineSegment(sketch, "E329", {"start": v(80.18, 2.35) * mm, "end": v(79.43, 2.33) * mm});
            skLineSegment(sketch, "E330", {"start": v(79.43, 2.33) * mm, "end": v(79.42, 2.77) * mm});
            skLineSegment(sketch, "E331", {"start": v(79.42, 2.77) * mm, "end": v(79.38, 3.61) * mm});
            skLineSegment(sketch, "E332", {"start": v(79.38, 3.61) * mm, "end": v(80.13, 3.65) * mm});
            skLineSegment(sketch, "E333", {"start": v(80.13, 3.65) * mm, "end": v(80.1, 4.2) * mm});
            skLineSegment(sketch, "E334", {"start": v(80.1, 4.2) * mm, "end": v(80.1, 4.35) * mm});
            skLineSegment(sketch, "E335", {"start": v(80.1, 4.35) * mm, "end": v(79.35, 4.31) * mm});
            skLineSegment(sketch, "E336", {"start": v(79.35, 4.31) * mm, "end": v(79.27, 5.59) * mm});
            skLineSegment(sketch, "E337", {"start": v(79.27, 5.59) * mm, "end": v(80.01, 5.65) * mm});
            skLineSegment(sketch, "E338", {"start": v(80.01, 5.65) * mm, "end": v(79.96, 6.34) * mm});
            skLineSegment(sketch, "E339", {"start": v(79.96, 6.34) * mm, "end": v(79.21, 6.29) * mm});
            skLineSegment(sketch, "E340", {"start": v(79.21, 6.29) * mm, "end": v(79.16, 6.93) * mm});
            skLineSegment(sketch, "E341", {"start": v(79.16, 6.93) * mm, "end": v(79.1, 7.56) * mm});
            skLineSegment(sketch, "E342", {"start": v(79.1, 7.56) * mm, "end": v(79.85, 7.64) * mm});
            skLineSegment(sketch, "E343", {"start": v(79.85, 7.64) * mm, "end": v(79.78, 8.33) * mm});
            skLineSegment(sketch, "E344", {"start": v(79.78, 8.33) * mm, "end": v(79.03, 8.26) * mm});
            skLineSegment(sketch, "E345", {"start": v(79.03, 8.26) * mm, "end": v(78.89, 9.53) * mm});
            skLineSegment(sketch, "E346", {"start": v(78.89, 9.53) * mm, "end": v(79.63, 9.63) * mm});
            skLineSegment(sketch, "E347", {"start": v(79.63, 9.63) * mm, "end": v(79.62, 9.78) * mm});
            skLineSegment(sketch, "E348", {"start": v(79.62, 9.78) * mm, "end": v(79.54, 10.32) * mm});
            skLineSegment(sketch, "E349", {"start": v(79.54, 10.32) * mm, "end": v(78.8, 10.23) * mm});
            skLineSegment(sketch, "E350", {"start": v(78.8, 10.23) * mm, "end": v(78.7, 11.06) * mm});
            skLineSegment(sketch, "E351", {"start": v(78.7, 11.06) * mm, "end": v(78.63, 11.5) * mm});
            skLineSegment(sketch, "E352", {"start": v(78.63, 11.5) * mm, "end": v(79.37, 11.6) * mm});
            skLineSegment(sketch, "E353", {"start": v(79.37, 11.6) * mm, "end": v(79.26, 12.3) * mm});
            skLineSegment(sketch, "E354", {"start": v(79.26, 12.3) * mm, "end": v(78.52, 12.19) * mm});
            skLineSegment(sketch, "E355", {"start": v(78.52, 12.19) * mm, "end": v(78.49, 12.43) * mm});
            skLineSegment(sketch, "E356", {"start": v(78.49, 12.43) * mm, "end": v(78.31, 13.45) * mm});
            skLineSegment(sketch, "E357", {"start": v(78.31, 13.45) * mm, "end": v(79.05, 13.58) * mm});
            skLineSegment(sketch, "E358", {"start": v(79.05, 13.58) * mm, "end": v(79, 13.93) * mm});
            skLineSegment(sketch, "E359", {"start": v(79, 13.93) * mm, "end": v(78.93, 14.27) * mm});
            skLineSegment(sketch, "E360", {"start": v(78.93, 14.27) * mm, "end": v(78.2, 14.14) * mm});
            skLineSegment(sketch, "E361", {"start": v(78.2, 14.14) * mm, "end": v(78, 15.16) * mm});
            skLineSegment(sketch, "E362", {"start": v(78, 15.16) * mm, "end": v(77.96, 15.4) * mm});
            skLineSegment(sketch, "E363", {"start": v(77.96, 15.4) * mm, "end": v(78.7, 15.55) * mm});
            skLineSegment(sketch, "E364", {"start": v(78.7, 15.55) * mm, "end": v(78.55, 16.24) * mm});
            skLineSegment(sketch, "E365", {"start": v(78.55, 16.24) * mm, "end": v(77.82, 16.09) * mm});
            skLineSegment(sketch, "E366", {"start": v(77.82, 16.09) * mm, "end": v(77.73, 16.52) * mm});
            skLineSegment(sketch, "E367", {"start": v(77.73, 16.52) * mm, "end": v(77.55, 17.34) * mm});
            skLineSegment(sketch, "E368", {"start": v(77.55, 17.34) * mm, "end": v(78.28, 17.5) * mm});
            skLineSegment(sketch, "E369", {"start": v(78.28, 17.5) * mm, "end": v(78.16, 18.04) * mm});
            skLineSegment(sketch, "E370", {"start": v(78.16, 18.04) * mm, "end": v(78.12, 18.2) * mm});
            skLineSegment(sketch, "E371", {"start": v(78.12, 18.2) * mm, "end": v(77.4, 18.02) * mm});
            skLineSegment(sketch, "E372", {"start": v(77.4, 18.02) * mm, "end": v(77.1, 19.27) * mm});
            skLineSegment(sketch, "E373", {"start": v(77.1, 19.27) * mm, "end": v(77.82, 19.45) * mm});
            skLineSegment(sketch, "E374", {"start": v(77.82, 19.45) * mm, "end": v(77.64, 20.13) * mm});
            skLineSegment(sketch, "E375", {"start": v(77.64, 20.13) * mm, "end": v(76.92, 19.95) * mm});
            skLineSegment(sketch, "E376", {"start": v(76.92, 19.95) * mm, "end": v(76.76, 20.57) * mm});
            skLineSegment(sketch, "E377", {"start": v(76.76, 20.57) * mm, "end": v(76.59, 21.18) * mm});
            skLineSegment(sketch, "E378", {"start": v(76.59, 21.18) * mm, "end": v(77.3, 21.39) * mm});
            skLineSegment(sketch, "E379", {"start": v(77.3, 21.39) * mm, "end": v(77.12, 22.06) * mm});
            skLineSegment(sketch, "E380", {"start": v(77.12, 22.06) * mm, "end": v(76.4, 21.86) * mm});
            skLineSegment(sketch, "E381", {"start": v(76.4, 21.86) * mm, "end": v(76.03, 23.09) * mm});
            skLineSegment(sketch, "E382", {"start": v(76.03, 23.09) * mm, "end": v(76.75, 23.3) * mm});
            skLineSegment(sketch, "E383", {"start": v(76.75, 23.3) * mm, "end": v(76.7, 23.45) * mm});
            skLineSegment(sketch, "E384", {"start": v(76.7, 23.45) * mm, "end": v(76.54, 23.98) * mm});
            skLineSegment(sketch, "E385", {"start": v(76.54, 23.98) * mm, "end": v(75.83, 23.76) * mm});
            skLineSegment(sketch, "E386", {"start": v(75.83, 23.76) * mm, "end": v(75.57, 24.56) * mm});
            skLineSegment(sketch, "E387", {"start": v(75.57, 24.56) * mm, "end": v(75.43, 24.98) * mm});
            skLineSegment(sketch, "E388", {"start": v(75.43, 24.98) * mm, "end": v(76.15, 25.21) * mm});
            skLineSegment(sketch, "E389", {"start": v(76.15, 25.21) * mm, "end": v(75.92, 25.88) * mm});
            skLineSegment(sketch, "E390", {"start": v(75.92, 25.88) * mm, "end": v(75.21, 25.64) * mm});
            skLineSegment(sketch, "E391", {"start": v(75.21, 25.64) * mm, "end": v(75.13, 25.87) * mm});
            skLineSegment(sketch, "E392", {"start": v(75.13, 25.87) * mm, "end": v(74.79, 26.85) * mm});
            skLineSegment(sketch, "E393", {"start": v(74.79, 26.85) * mm, "end": v(75.5, 27.1) * mm});
            skLineSegment(sketch, "E394", {"start": v(75.5, 27.1) * mm, "end": v(75.38, 27.43) * mm});
            skLineSegment(sketch, "E395", {"start": v(75.38, 27.43) * mm, "end": v(75.25, 27.76) * mm});
            skLineSegment(sketch, "E396", {"start": v(75.25, 27.76) * mm, "end": v(74.55, 27.5) * mm});
            skLineSegment(sketch, "E397", {"start": v(74.55, 27.5) * mm, "end": v(74.19, 28.48) * mm});
            skLineSegment(sketch, "E398", {"start": v(74.19, 28.48) * mm, "end": v(74.1, 28.7) * mm});
            skLineSegment(sketch, "E399", {"start": v(74.1, 28.7) * mm, "end": v(74.8, 28.98) * mm});
            skLineSegment(sketch, "E400", {"start": v(74.8, 28.98) * mm, "end": v(74.54, 29.63) * mm});
            skLineSegment(sketch, "E401", {"start": v(74.54, 29.63) * mm, "end": v(73.84, 29.36) * mm});
            skLineSegment(sketch, "E402", {"start": v(73.84, 29.36) * mm, "end": v(73.68, 29.77) * mm});
            skLineSegment(sketch, "E403", {"start": v(73.68, 29.77) * mm, "end": v(73.36, 30.54) * mm});
            skLineSegment(sketch, "E404", {"start": v(73.36, 30.54) * mm, "end": v(74.05, 30.83) * mm});
            skLineSegment(sketch, "E405", {"start": v(74.05, 30.83) * mm, "end": v(73.84, 31.34) * mm});
            skLineSegment(sketch, "E406", {"start": v(73.84, 31.34) * mm, "end": v(73.78, 31.48) * mm});
            skLineSegment(sketch, "E407", {"start": v(73.78, 31.48) * mm, "end": v(73.09, 31.19) * mm});
            skLineSegment(sketch, "E408", {"start": v(73.09, 31.19) * mm, "end": v(72.57, 32.36) * mm});
            skLineSegment(sketch, "E409", {"start": v(72.57, 32.36) * mm, "end": v(73.26, 32.67) * mm});
            skLineSegment(sketch, "E410", {"start": v(73.26, 32.67) * mm, "end": v(72.97, 33.3) * mm});
            skLineSegment(sketch, "E411", {"start": v(72.97, 33.3) * mm, "end": v(72.28, 33) * mm});
            skLineSegment(sketch, "E412", {"start": v(72.28, 33) * mm, "end": v(72.02, 33.58) * mm});
            skLineSegment(sketch, "E413", {"start": v(72.02, 33.58) * mm, "end": v(71.74, 34.16) * mm});
            skLineSegment(sketch, "E414", {"start": v(71.74, 34.16) * mm, "end": v(72.42, 34.49) * mm});
            skLineSegment(sketch, "E415", {"start": v(72.42, 34.49) * mm, "end": v(72.12, 35.12) * mm});
            skLineSegment(sketch, "E416", {"start": v(72.12, 35.12) * mm, "end": v(71.44, 34.8) * mm});
            skLineSegment(sketch, "E417", {"start": v(71.44, 34.8) * mm, "end": v(70.87, 35.94) * mm});
            skLineSegment(sketch, "E418", {"start": v(70.87, 35.94) * mm, "end": v(71.54, 36.28) * mm});
            skLineSegment(sketch, "E419", {"start": v(71.54, 36.28) * mm, "end": v(71.47, 36.42) * mm});
            skLineSegment(sketch, "E420", {"start": v(71.47, 36.42) * mm, "end": v(71.22, 36.9) * mm});
            skLineSegment(sketch, "E421", {"start": v(71.22, 36.9) * mm, "end": v(70.55, 36.56) * mm});
            skLineSegment(sketch, "E422", {"start": v(70.55, 36.56) * mm, "end": v(70.16, 37.3) * mm});
            skLineSegment(sketch, "E423", {"start": v(70.16, 37.3) * mm, "end": v(69.95, 37.7) * mm});
            skLineSegment(sketch, "E424", {"start": v(69.95, 37.7) * mm, "end": v(70.61, 38.05) * mm});
            skLineSegment(sketch, "E425", {"start": v(70.61, 38.05) * mm, "end": v(70.28, 38.67) * mm});
            skLineSegment(sketch, "E426", {"start": v(70.28, 38.67) * mm, "end": v(69.62, 38.31) * mm});
            skLineSegment(sketch, "E427", {"start": v(69.62, 38.31) * mm, "end": v(69.5, 38.52) * mm});
            skLineSegment(sketch, "E428", {"start": v(69.5, 38.52) * mm, "end": v(69, 39.43) * mm});
            skLineSegment(sketch, "E429", {"start": v(69, 39.43) * mm, "end": v(69.64, 39.8) * mm});
            skLineSegment(sketch, "E430", {"start": v(69.64, 39.8) * mm, "end": v(69.47, 40.1) * mm});
            skLineSegment(sketch, "E431", {"start": v(69.47, 40.1) * mm, "end": v(69.29, 40.4) * mm});
            skLineSegment(sketch, "E432", {"start": v(69.29, 40.4) * mm, "end": v(68.64, 40.03) * mm});
            skLineSegment(sketch, "E433", {"start": v(68.64, 40.03) * mm, "end": v(68.11, 40.93) * mm});
            skLineSegment(sketch, "E434", {"start": v(68.11, 40.93) * mm, "end": v(67.99, 41.14) * mm});
            skLineSegment(sketch, "E435", {"start": v(67.99, 41.14) * mm, "end": v(68.63, 41.53) * mm});
            skLineSegment(sketch, "E436", {"start": v(68.63, 41.53) * mm, "end": v(68.26, 42.12) * mm});
            skLineSegment(sketch, "E437", {"start": v(68.26, 42.12) * mm, "end": v(67.62, 41.73) * mm});
            skLineSegment(sketch, "E438", {"start": v(67.62, 41.73) * mm, "end": v(67.39, 42.1) * mm});
            skLineSegment(sketch, "E439", {"start": v(67.39, 42.1) * mm, "end": v(66.94, 42.82) * mm});
            skLineSegment(sketch, "E440", {"start": v(66.94, 42.82) * mm, "end": v(67.57, 43.22) * mm});
            skLineSegment(sketch, "E441", {"start": v(67.57, 43.22) * mm, "end": v(67.27, 43.69) * mm});
            skLineSegment(sketch, "E442", {"start": v(67.27, 43.69) * mm, "end": v(67.2, 43.81) * mm});
            skLineSegment(sketch, "E443", {"start": v(67.2, 43.81) * mm, "end": v(66.56, 43.4) * mm});
            skLineSegment(sketch, "E444", {"start": v(66.56, 43.4) * mm, "end": v(65.85, 44.47) * mm});
            skLineSegment(sketch, "E445", {"start": v(65.85, 44.47) * mm, "end": v(66.47, 44.9) * mm});
            skLineSegment(sketch, "E446", {"start": v(66.47, 44.9) * mm, "end": v(66.08, 45.47) * mm});
            skLineSegment(sketch, "E447", {"start": v(66.08, 45.47) * mm, "end": v(65.46, 45.05) * mm});
            skLineSegment(sketch, "E448", {"start": v(65.46, 45.05) * mm, "end": v(65.1, 45.58) * mm});
            skLineSegment(sketch, "E449", {"start": v(65.1, 45.58) * mm, "end": v(64.72, 46.1) * mm});
            skLineSegment(sketch, "E450", {"start": v(64.72, 46.1) * mm, "end": v(65.33, 46.54) * mm});
            skLineSegment(sketch, "E451", {"start": v(65.33, 46.54) * mm, "end": v(64.92, 47.1) * mm});
            skLineSegment(sketch, "E452", {"start": v(64.92, 47.1) * mm, "end": v(64.31, 46.67) * mm});
            skLineSegment(sketch, "E453", {"start": v(64.31, 46.67) * mm, "end": v(63.55, 47.7) * mm});
            skLineSegment(sketch, "E454", {"start": v(63.55, 47.7) * mm, "end": v(64.15, 48.15) * mm});
            skLineSegment(sketch, "E455", {"start": v(64.15, 48.15) * mm, "end": v(64.06, 48.27) * mm});
            skLineSegment(sketch, "E456", {"start": v(64.06, 48.27) * mm, "end": v(63.73, 48.71) * mm});
            skLineSegment(sketch, "E457", {"start": v(63.73, 48.71) * mm, "end": v(63.13, 48.26) * mm});
            skLineSegment(sketch, "E458", {"start": v(63.13, 48.26) * mm, "end": v(62.62, 48.92) * mm});
            skLineSegment(sketch, "E459", {"start": v(62.62, 48.92) * mm, "end": v(62.34, 49.27) * mm});
            skLineSegment(sketch, "E460", {"start": v(62.34, 49.27) * mm, "end": v(62.93, 49.74) * mm});
            skLineSegment(sketch, "E461", {"start": v(62.93, 49.74) * mm, "end": v(62.5, 50.28) * mm});
            skLineSegment(sketch, "E462", {"start": v(62.5, 50.28) * mm, "end": v(61.9, 49.82) * mm});
            skLineSegment(sketch, "E463", {"start": v(61.9, 49.82) * mm, "end": v(61.76, 50) * mm});
            skLineSegment(sketch, "E464", {"start": v(61.76, 50) * mm, "end": v(61.1, 50.8) * mm});
            skLineSegment(sketch, "E465", {"start": v(61.1, 50.8) * mm, "end": v(61.67, 51.3) * mm});
            skLineSegment(sketch, "E466", {"start": v(61.67, 51.3) * mm, "end": v(61.45, 51.56) * mm});
            skLineSegment(sketch, "E467", {"start": v(61.45, 51.56) * mm, "end": v(61.22, 51.83) * mm});
            skLineSegment(sketch, "E468", {"start": v(61.22, 51.83) * mm, "end": v(60.65, 51.34) * mm});
            skLineSegment(sketch, "E469", {"start": v(60.65, 51.34) * mm, "end": v(59.97, 52.13) * mm});
            skLineSegment(sketch, "E470", {"start": v(59.97, 52.13) * mm, "end": v(59.81, 52.32) * mm});
            skLineSegment(sketch, "E471", {"start": v(59.81, 52.32) * mm, "end": v(60.37, 52.81) * mm});
            skLineSegment(sketch, "E472", {"start": v(60.37, 52.81) * mm, "end": v(59.9, 53.34) * mm});
            skLineSegment(sketch, "E473", {"start": v(59.9, 53.34) * mm, "end": v(59.35, 52.84) * mm});
            skLineSegment(sketch, "E474", {"start": v(59.35, 52.84) * mm, "end": v(59.05, 53.17) * mm});
            skLineSegment(sketch, "E475", {"start": v(59.05, 53.17) * mm, "end": v(58.49, 53.8) * mm});
            skLineSegment(sketch, "E476", {"start": v(58.49, 53.8) * mm, "end": v(59.04, 54.3) * mm});
            skLineSegment(sketch, "E477", {"start": v(59.04, 54.3) * mm, "end": v(58.66, 54.7) * mm});
            skLineSegment(sketch, "E478", {"start": v(58.66, 54.7) * mm, "end": v(58.56, 54.81) * mm});
            skLineSegment(sketch, "E479", {"start": v(58.56, 54.81) * mm, "end": v(58.01, 54.3) * mm});
            skLineSegment(sketch, "E480", {"start": v(58.01, 54.3) * mm, "end": v(57.13, 55.23) * mm});
            skLineSegment(sketch, "E481", {"start": v(57.13, 55.23) * mm, "end": v(57.67, 55.76) * mm});
            skLineSegment(sketch, "E482", {"start": v(57.67, 55.76) * mm, "end": v(57.18, 56.26) * mm});
            skLineSegment(sketch, "E483", {"start": v(57.18, 56.26) * mm, "end": v(56.64, 55.73) * mm});
            skLineSegment(sketch, "E484", {"start": v(56.64, 55.73) * mm, "end": v(56.19, 56.19) * mm});
            skLineSegment(sketch, "E485", {"start": v(56.19, 56.19) * mm, "end": v(55.73, 56.64) * mm});
            skLineSegment(sketch, "E486", {"start": v(55.73, 56.64) * mm, "end": v(56.26, 57.18) * mm});
            skLineSegment(sketch, "E487", {"start": v(56.26, 57.18) * mm, "end": v(55.76, 57.67) * mm});
            skLineSegment(sketch, "E488", {"start": v(55.76, 57.67) * mm, "end": v(55.23, 57.13) * mm});
            skLineSegment(sketch, "E489", {"start": v(55.23, 57.13) * mm, "end": v(54.3, 58.01) * mm});
            skLineSegment(sketch, "E490", {"start": v(54.3, 58.01) * mm, "end": v(54.81, 58.56) * mm});
            skLineSegment(sketch, "E491", {"start": v(54.81, 58.56) * mm, "end": v(54.7, 58.66) * mm});
            skLineSegment(sketch, "E492", {"start": v(54.7, 58.66) * mm, "end": v(54.3, 59.04) * mm});
            skLineSegment(sketch, "E493", {"start": v(54.3, 59.04) * mm, "end": v(53.8, 58.49) * mm});
            skLineSegment(sketch, "E494", {"start": v(53.8, 58.49) * mm, "end": v(53.17, 59.05) * mm});
            skLineSegment(sketch, "E495", {"start": v(53.17, 59.05) * mm, "end": v(52.84, 59.35) * mm});
            skLineSegment(sketch, "E496", {"start": v(52.84, 59.35) * mm, "end": v(53.34, 59.9) * mm});
            skLineSegment(sketch, "E497", {"start": v(53.34, 59.9) * mm, "end": v(52.81, 60.37) * mm});
            skLineSegment(sketch, "E498", {"start": v(52.81, 60.37) * mm, "end": v(52.32, 59.81) * mm});
            skLineSegment(sketch, "E499", {"start": v(52.32, 59.81) * mm, "end": v(52.13, 59.97) * mm});
            skLineSegment(sketch, "E500", {"start": v(52.13, 59.97) * mm, "end": v(51.34, 60.65) * mm});
            skLineSegment(sketch, "E501", {"start": v(51.34, 60.65) * mm, "end": v(51.83, 61.22) * mm});
            skLineSegment(sketch, "E502", {"start": v(51.83, 61.22) * mm, "end": v(51.56, 61.45) * mm});
            skLineSegment(sketch, "E503", {"start": v(51.56, 61.45) * mm, "end": v(51.3, 61.67) * mm});
            skLineSegment(sketch, "E504", {"start": v(51.3, 61.67) * mm, "end": v(50.8, 61.1) * mm});
            skLineSegment(sketch, "E505", {"start": v(50.8, 61.1) * mm, "end": v(50, 61.76) * mm});
            skLineSegment(sketch, "E506", {"start": v(50, 61.76) * mm, "end": v(49.82, 61.9) * mm});
            skLineSegment(sketch, "E507", {"start": v(49.82, 61.9) * mm, "end": v(50.28, 62.5) * mm});
            skLineSegment(sketch, "E508", {"start": v(50.28, 62.5) * mm, "end": v(49.74, 62.93) * mm});
            skLineSegment(sketch, "E509", {"start": v(49.74, 62.93) * mm, "end": v(49.27, 62.34) * mm});
            skLineSegment(sketch, "E510", {"start": v(49.27, 62.34) * mm, "end": v(48.92, 62.62) * mm});
            skLineSegment(sketch, "E511", {"start": v(48.92, 62.62) * mm, "end": v(48.26, 63.13) * mm});
            skLineSegment(sketch, "E512", {"start": v(48.26, 63.13) * mm, "end": v(48.71, 63.73) * mm});
            skLineSegment(sketch, "E513", {"start": v(48.71, 63.73) * mm, "end": v(48.27, 64.06) * mm});
            skLineSegment(sketch, "E514", {"start": v(48.27, 64.06) * mm, "end": v(48.15, 64.15) * mm});
            skLineSegment(sketch, "E515", {"start": v(48.15, 64.15) * mm, "end": v(47.7, 63.55) * mm});
            skLineSegment(sketch, "E516", {"start": v(47.7, 63.55) * mm, "end": v(46.67, 64.31) * mm});
            skLineSegment(sketch, "E517", {"start": v(46.67, 64.31) * mm, "end": v(47.1, 64.92) * mm});
            skLineSegment(sketch, "E518", {"start": v(47.1, 64.92) * mm, "end": v(46.54, 65.33) * mm});
            skLineSegment(sketch, "E519", {"start": v(46.54, 65.33) * mm, "end": v(46.1, 64.72) * mm});
            skLineSegment(sketch, "E520", {"start": v(46.1, 64.72) * mm, "end": v(45.58, 65.1) * mm});
            skLineSegment(sketch, "E521", {"start": v(45.58, 65.1) * mm, "end": v(45.05, 65.46) * mm});
            skLineSegment(sketch, "E522", {"start": v(45.05, 65.46) * mm, "end": v(45.47, 66.08) * mm});
            skLineSegment(sketch, "E523", {"start": v(45.47, 66.08) * mm, "end": v(44.9, 66.47) * mm});
            skLineSegment(sketch, "E524", {"start": v(44.9, 66.47) * mm, "end": v(44.47, 65.85) * mm});
            skLineSegment(sketch, "E525", {"start": v(44.47, 65.85) * mm, "end": v(43.4, 66.56) * mm});
            skLineSegment(sketch, "E526", {"start": v(43.4, 66.56) * mm, "end": v(43.81, 67.2) * mm});
            skLineSegment(sketch, "E527", {"start": v(43.81, 67.2) * mm, "end": v(43.69, 67.27) * mm});
            skLineSegment(sketch, "E528", {"start": v(43.69, 67.27) * mm, "end": v(43.22, 67.57) * mm});
            skLineSegment(sketch, "E529", {"start": v(43.22, 67.57) * mm, "end": v(42.82, 66.94) * mm});
            skLineSegment(sketch, "E530", {"start": v(42.82, 66.94) * mm, "end": v(42.1, 67.39) * mm});
            skLineSegment(sketch, "E531", {"start": v(42.1, 67.39) * mm, "end": v(41.73, 67.62) * mm});
            skLineSegment(sketch, "E532", {"start": v(41.73, 67.62) * mm, "end": v(42.12, 68.26) * mm});
            skLineSegment(sketch, "E533", {"start": v(42.12, 68.26) * mm, "end": v(41.53, 68.63) * mm});
            skLineSegment(sketch, "E534", {"start": v(41.53, 68.63) * mm, "end": v(41.14, 67.99) * mm});
            skLineSegment(sketch, "E535", {"start": v(41.14, 67.99) * mm, "end": v(40.93, 68.11) * mm});
            skLineSegment(sketch, "E536", {"start": v(40.93, 68.11) * mm, "end": v(40.03, 68.64) * mm});
            skLineSegment(sketch, "E537", {"start": v(40.03, 68.64) * mm, "end": v(40.4, 69.29) * mm});
            skLineSegment(sketch, "E538", {"start": v(40.4, 69.29) * mm, "end": v(40.1, 69.47) * mm});
            skLineSegment(sketch, "E539", {"start": v(40.1, 69.47) * mm, "end": v(39.8, 69.64) * mm});
            skLineSegment(sketch, "E540", {"start": v(39.8, 69.64) * mm, "end": v(39.43, 69) * mm});
            skLineSegment(sketch, "E541", {"start": v(39.43, 69) * mm, "end": v(38.52, 69.5) * mm});
            skLineSegment(sketch, "E542", {"start": v(38.52, 69.5) * mm, "end": v(38.31, 69.62) * mm});
            skLineSegment(sketch, "E543", {"start": v(38.31, 69.62) * mm, "end": v(38.67, 70.28) * mm});
            skLineSegment(sketch, "E544", {"start": v(38.67, 70.28) * mm, "end": v(38.05, 70.61) * mm});
            skLineSegment(sketch, "E545", {"start": v(38.05, 70.61) * mm, "end": v(37.7, 69.95) * mm});
            skLineSegment(sketch, "E546", {"start": v(37.7, 69.95) * mm, "end": v(37.3, 70.16) * mm});
            skLineSegment(sketch, "E547", {"start": v(37.3, 70.16) * mm, "end": v(36.56, 70.55) * mm});
            skLineSegment(sketch, "E548", {"start": v(36.56, 70.55) * mm, "end": v(36.9, 71.22) * mm});
            skLineSegment(sketch, "E549", {"start": v(36.9, 71.22) * mm, "end": v(36.42, 71.47) * mm});
            skLineSegment(sketch, "E550", {"start": v(36.42, 71.47) * mm, "end": v(36.28, 71.54) * mm});
            skLineSegment(sketch, "E551", {"start": v(36.28, 71.54) * mm, "end": v(35.94, 70.87) * mm});
            skLineSegment(sketch, "E552", {"start": v(35.94, 70.87) * mm, "end": v(34.8, 71.44) * mm});
            skLineSegment(sketch, "E553", {"start": v(34.8, 71.44) * mm, "end": v(35.12, 72.12) * mm});
            skLineSegment(sketch, "E554", {"start": v(35.12, 72.12) * mm, "end": v(34.49, 72.42) * mm});
            skLineSegment(sketch, "E555", {"start": v(34.49, 72.42) * mm, "end": v(34.16, 71.74) * mm});
            skLineSegment(sketch, "E556", {"start": v(34.16, 71.74) * mm, "end": v(33.58, 72.02) * mm});
            skLineSegment(sketch, "E557", {"start": v(33.58, 72.02) * mm, "end": v(33, 72.28) * mm});
            skLineSegment(sketch, "E558", {"start": v(33, 72.28) * mm, "end": v(33.3, 72.97) * mm});
            skLineSegment(sketch, "E559", {"start": v(33.3, 72.97) * mm, "end": v(32.67, 73.26) * mm});
            skLineSegment(sketch, "E560", {"start": v(32.67, 73.26) * mm, "end": v(32.36, 72.57) * mm});
            skLineSegment(sketch, "E561", {"start": v(32.36, 72.57) * mm, "end": v(31.19, 73.09) * mm});
            skLineSegment(sketch, "E562", {"start": v(31.19, 73.09) * mm, "end": v(31.48, 73.78) * mm});
            skLineSegment(sketch, "E563", {"start": v(31.48, 73.78) * mm, "end": v(31.34, 73.84) * mm});
            skLineSegment(sketch, "E564", {"start": v(31.34, 73.84) * mm, "end": v(30.83, 74.05) * mm});
            skLineSegment(sketch, "E565", {"start": v(30.83, 74.05) * mm, "end": v(30.54, 73.36) * mm});
            skLineSegment(sketch, "E566", {"start": v(30.54, 73.36) * mm, "end": v(29.77, 73.68) * mm});
            skLineSegment(sketch, "E567", {"start": v(29.77, 73.68) * mm, "end": v(29.36, 73.84) * mm});
            skLineSegment(sketch, "E568", {"start": v(29.36, 73.84) * mm, "end": v(29.63, 74.54) * mm});
            skLineSegment(sketch, "E569", {"start": v(29.63, 74.54) * mm, "end": v(28.98, 74.8) * mm});
            skLineSegment(sketch, "E570", {"start": v(28.98, 74.8) * mm, "end": v(28.7, 74.1) * mm});
            skLineSegment(sketch, "E571", {"start": v(28.7, 74.1) * mm, "end": v(28.48, 74.19) * mm});
            skLineSegment(sketch, "E572", {"start": v(28.48, 74.19) * mm, "end": v(27.5, 74.55) * mm});
            skLineSegment(sketch, "E573", {"start": v(27.5, 74.55) * mm, "end": v(27.76, 75.25) * mm});
            skLineSegment(sketch, "E574", {"start": v(27.76, 75.25) * mm, "end": v(27.43, 75.38) * mm});
            skLineSegment(sketch, "E575", {"start": v(27.43, 75.38) * mm, "end": v(27.1, 75.5) * mm});
            skLineSegment(sketch, "E576", {"start": v(27.1, 75.5) * mm, "end": v(26.85, 74.79) * mm});
            skLineSegment(sketch, "E577", {"start": v(26.85, 74.79) * mm, "end": v(25.87, 75.13) * mm});
            skLineSegment(sketch, "E578", {"start": v(25.87, 75.13) * mm, "end": v(25.64, 75.21) * mm});
            skLineSegment(sketch, "E579", {"start": v(25.64, 75.21) * mm, "end": v(25.88, 75.92) * mm});
            skLineSegment(sketch, "E580", {"start": v(25.88, 75.92) * mm, "end": v(25.21, 76.15) * mm});
            skLineSegment(sketch, "E581", {"start": v(25.21, 76.15) * mm, "end": v(24.98, 75.43) * mm});
            skLineSegment(sketch, "E582", {"start": v(24.98, 75.43) * mm, "end": v(24.56, 75.57) * mm});
            skLineSegment(sketch, "E583", {"start": v(24.56, 75.57) * mm, "end": v(23.76, 75.83) * mm});
            skLineSegment(sketch, "E584", {"start": v(23.76, 75.83) * mm, "end": v(23.98, 76.54) * mm});
            skLineSegment(sketch, "E585", {"start": v(23.98, 76.54) * mm, "end": v(23.45, 76.7) * mm});
            skLineSegment(sketch, "E586", {"start": v(23.45, 76.7) * mm, "end": v(23.3, 76.75) * mm});
            skLineSegment(sketch, "E587", {"start": v(23.3, 76.75) * mm, "end": v(23.09, 76.03) * mm});
            skLineSegment(sketch, "E588", {"start": v(23.09, 76.03) * mm, "end": v(21.86, 76.4) * mm});
            skLineSegment(sketch, "E589", {"start": v(21.86, 76.4) * mm, "end": v(22.06, 77.12) * mm});
            skLineSegment(sketch, "E590", {"start": v(22.06, 77.12) * mm, "end": v(21.39, 77.3) * mm});
            skLineSegment(sketch, "E591", {"start": v(21.39, 77.3) * mm, "end": v(21.18, 76.59) * mm});
            skLineSegment(sketch, "E592", {"start": v(21.18, 76.59) * mm, "end": v(20.57, 76.76) * mm});
            skLineSegment(sketch, "E593", {"start": v(20.57, 76.76) * mm, "end": v(19.95, 76.92) * mm});
            skLineSegment(sketch, "E594", {"start": v(19.95, 76.92) * mm, "end": v(20.13, 77.64) * mm});
            skLineSegment(sketch, "E595", {"start": v(20.13, 77.64) * mm, "end": v(19.45, 77.82) * mm});
            skLineSegment(sketch, "E596", {"start": v(19.45, 77.82) * mm, "end": v(19.27, 77.1) * mm});
            skLineSegment(sketch, "E597", {"start": v(19.27, 77.1) * mm, "end": v(18.02, 77.4) * mm});
            skLineSegment(sketch, "E598", {"start": v(18.02, 77.4) * mm, "end": v(18.2, 78.12) * mm});
            skLineSegment(sketch, "E599", {"start": v(18.2, 78.12) * mm, "end": v(18.04, 78.16) * mm});
            skLineSegment(sketch, "E600", {"start": v(18.04, 78.16) * mm, "end": v(17.5, 78.28) * mm});
            skLineSegment(sketch, "E601", {"start": v(17.5, 78.28) * mm, "end": v(17.34, 77.55) * mm});
            skLineSegment(sketch, "E602", {"start": v(17.34, 77.55) * mm, "end": v(16.52, 77.73) * mm});
            skLineSegment(sketch, "E603", {"start": v(16.52, 77.73) * mm, "end": v(16.09, 77.82) * mm});
            skLineSegment(sketch, "E604", {"start": v(16.09, 77.82) * mm, "end": v(16.24, 78.55) * mm});
            skLineSegment(sketch, "E605", {"start": v(16.24, 78.55) * mm, "end": v(15.55, 78.7) * mm});
            skLineSegment(sketch, "E606", {"start": v(15.55, 78.7) * mm, "end": v(15.4, 77.96) * mm});
            skLineSegment(sketch, "E607", {"start": v(15.4, 77.96) * mm, "end": v(15.16, 78) * mm});
            skLineSegment(sketch, "E608", {"start": v(15.16, 78) * mm, "end": v(14.14, 78.2) * mm});
            skLineSegment(sketch, "E609", {"start": v(14.14, 78.2) * mm, "end": v(14.27, 78.93) * mm});
            skLineSegment(sketch, "E610", {"start": v(14.27, 78.93) * mm, "end": v(13.93, 79) * mm});
            skLineSegment(sketch, "E611", {"start": v(13.93, 79) * mm, "end": v(13.58, 79.05) * mm});
            skLineSegment(sketch, "E612", {"start": v(13.58, 79.05) * mm, "end": v(13.45, 78.31) * mm});
            skLineSegment(sketch, "E613", {"start": v(13.45, 78.31) * mm, "end": v(12.43, 78.49) * mm});
            skLineSegment(sketch, "E614", {"start": v(12.43, 78.49) * mm, "end": v(12.19, 78.52) * mm});
            skLineSegment(sketch, "E615", {"start": v(12.19, 78.52) * mm, "end": v(12.3, 79.26) * mm});
            skLineSegment(sketch, "E616", {"start": v(12.3, 79.26) * mm, "end": v(11.6, 79.37) * mm});
            skLineSegment(sketch, "E617", {"start": v(11.6, 79.37) * mm, "end": v(11.5, 78.63) * mm});
            skLineSegment(sketch, "E618", {"start": v(11.5, 78.63) * mm, "end": v(11.06, 78.7) * mm});
            skLineSegment(sketch, "E619", {"start": v(11.06, 78.7) * mm, "end": v(10.23, 78.8) * mm});
            skLineSegment(sketch, "E620", {"start": v(10.23, 78.8) * mm, "end": v(10.32, 79.54) * mm});
            skLineSegment(sketch, "E621", {"start": v(10.32, 79.54) * mm, "end": v(9.78, 79.62) * mm});
            skLineSegment(sketch, "E622", {"start": v(9.78, 79.62) * mm, "end": v(9.63, 79.63) * mm});
            skLineSegment(sketch, "E623", {"start": v(9.63, 79.63) * mm, "end": v(9.53, 78.89) * mm});
            skLineSegment(sketch, "E624", {"start": v(9.53, 78.89) * mm, "end": v(8.26, 79.03) * mm});
            skLineSegment(sketch, "E625", {"start": v(8.26, 79.03) * mm, "end": v(8.33, 79.78) * mm});
            skLineSegment(sketch, "E626", {"start": v(8.33, 79.78) * mm, "end": v(7.64, 79.85) * mm});
            skLineSegment(sketch, "E627", {"start": v(7.64, 79.85) * mm, "end": v(7.56, 79.1) * mm});
            skLineSegment(sketch, "E628", {"start": v(7.56, 79.1) * mm, "end": v(6.93, 79.16) * mm});
            skLineSegment(sketch, "E629", {"start": v(6.93, 79.16) * mm, "end": v(6.29, 79.21) * mm});
            skLineSegment(sketch, "E630", {"start": v(6.29, 79.21) * mm, "end": v(6.34, 79.96) * mm});
            skLineSegment(sketch, "E631", {"start": v(6.34, 79.96) * mm, "end": v(5.65, 80.01) * mm});
            skLineSegment(sketch, "E632", {"start": v(5.65, 80.01) * mm, "end": v(5.59, 79.27) * mm});
            skLineSegment(sketch, "E633", {"start": v(5.59, 79.27) * mm, "end": v(4.31, 79.35) * mm});
            skLineSegment(sketch, "E634", {"start": v(4.31, 79.35) * mm, "end": v(4.35, 80.1) * mm});
            skLineSegment(sketch, "E635", {"start": v(4.35, 80.1) * mm, "end": v(4.2, 80.1) * mm});
            skLineSegment(sketch, "E636", {"start": v(4.2, 80.1) * mm, "end": v(3.65, 80.13) * mm});
            skLineSegment(sketch, "E637", {"start": v(3.65, 80.13) * mm, "end": v(3.61, 79.38) * mm});
            skLineSegment(sketch, "E638", {"start": v(3.61, 79.38) * mm, "end": v(2.77, 79.42) * mm});
            skLineSegment(sketch, "E639", {"start": v(2.77, 79.42) * mm, "end": v(2.33, 79.43) * mm});
            skLineSegment(sketch, "E640", {"start": v(2.33, 79.43) * mm, "end": v(2.35, 80.18) * mm});
            skLineSegment(sketch, "E641", {"start": v(2.35, 80.18) * mm, "end": v(1.65, 80.2) * mm});
            skLineSegment(sketch, "E642", {"start": v(1.65, 80.2) * mm, "end": v(1.63, 79.45) * mm});
            skLineSegment(sketch, "E643", {"start": v(1.63, 79.45) * mm, "end": v(1.39, 79.45) * mm});
            skLineSegment(sketch, "E644", {"start": v(1.39, 79.45) * mm, "end": v(0.35, 79.46) * mm});
            skLineSegment(sketch, "E645", {"start": v(0.35, 79.46) * mm, "end": v(0.35, 80.21) * mm});
            skLineSegment(sketch, "E646", {"start": v(0.35, 80.21) * mm, "end": v(0, 80.21) * mm});
            skLineSegment(sketch, "E647", {"start": v(0, 80.21) * mm, "end": v(-0.35, 80.21) * mm});
            skLineSegment(sketch, "E648", {"start": v(-0.35, 80.21) * mm, "end": v(-0.35, 79.46) * mm});
            skLineSegment(sketch, "E649", {"start": v(-0.35, 79.46) * mm, "end": v(-1.39, 79.45) * mm});
            skLineSegment(sketch, "E650", {"start": v(-1.39, 79.45) * mm, "end": v(-1.63, 79.45) * mm});
            skLineSegment(sketch, "E651", {"start": v(-1.63, 79.45) * mm, "end": v(-1.65, 80.2) * mm});
            skLineSegment(sketch, "E652", {"start": v(-1.65, 80.2) * mm, "end": v(-2.35, 80.18) * mm});
            skLineSegment(sketch, "E653", {"start": v(-2.35, 80.18) * mm, "end": v(-2.33, 79.43) * mm});
            skLineSegment(sketch, "E654", {"start": v(-2.33, 79.43) * mm, "end": v(-2.77, 79.42) * mm});
            skLineSegment(sketch, "E655", {"start": v(-2.77, 79.42) * mm, "end": v(-3.61, 79.38) * mm});
            skLineSegment(sketch, "E656", {"start": v(-3.61, 79.38) * mm, "end": v(-3.65, 80.13) * mm});
            skLineSegment(sketch, "E657", {"start": v(-3.65, 80.13) * mm, "end": v(-4.2, 80.1) * mm});
            skLineSegment(sketch, "E658", {"start": v(-4.2, 80.1) * mm, "end": v(-4.35, 80.1) * mm});
            skLineSegment(sketch, "E659", {"start": v(-4.35, 80.1) * mm, "end": v(-4.31, 79.35) * mm});
            skLineSegment(sketch, "E660", {"start": v(-4.31, 79.35) * mm, "end": v(-5.59, 79.27) * mm});
            skLineSegment(sketch, "E661", {"start": v(-5.59, 79.27) * mm, "end": v(-5.65, 80.01) * mm});
            skLineSegment(sketch, "E662", {"start": v(-5.65, 80.01) * mm, "end": v(-6.34, 79.96) * mm});
            skLineSegment(sketch, "E663", {"start": v(-6.34, 79.96) * mm, "end": v(-6.29, 79.21) * mm});
            skLineSegment(sketch, "E664", {"start": v(-6.29, 79.21) * mm, "end": v(-6.93, 79.16) * mm});
            skLineSegment(sketch, "E665", {"start": v(-6.93, 79.16) * mm, "end": v(-7.56, 79.1) * mm});
            skLineSegment(sketch, "E666", {"start": v(-7.56, 79.1) * mm, "end": v(-7.64, 79.85) * mm});
            skLineSegment(sketch, "E667", {"start": v(-7.64, 79.85) * mm, "end": v(-8.33, 79.78) * mm});
            skLineSegment(sketch, "E668", {"start": v(-8.33, 79.78) * mm, "end": v(-8.26, 79.03) * mm});
            skLineSegment(sketch, "E669", {"start": v(-8.26, 79.03) * mm, "end": v(-9.53, 78.89) * mm});
            skLineSegment(sketch, "E670", {"start": v(-9.53, 78.89) * mm, "end": v(-9.63, 79.63) * mm});
            skLineSegment(sketch, "E671", {"start": v(-9.63, 79.63) * mm, "end": v(-9.78, 79.62) * mm});
            skLineSegment(sketch, "E672", {"start": v(-9.78, 79.62) * mm, "end": v(-10.32, 79.54) * mm});
            skLineSegment(sketch, "E673", {"start": v(-10.32, 79.54) * mm, "end": v(-10.23, 78.8) * mm});
            skLineSegment(sketch, "E674", {"start": v(-10.23, 78.8) * mm, "end": v(-11.06, 78.7) * mm});
            skLineSegment(sketch, "E675", {"start": v(-11.06, 78.7) * mm, "end": v(-11.5, 78.63) * mm});
            skLineSegment(sketch, "E676", {"start": v(-11.5, 78.63) * mm, "end": v(-11.6, 79.37) * mm});
            skLineSegment(sketch, "E677", {"start": v(-11.6, 79.37) * mm, "end": v(-12.3, 79.26) * mm});
            skLineSegment(sketch, "E678", {"start": v(-12.3, 79.26) * mm, "end": v(-12.19, 78.52) * mm});
            skLineSegment(sketch, "E679", {"start": v(-12.19, 78.52) * mm, "end": v(-12.43, 78.49) * mm});
            skLineSegment(sketch, "E680", {"start": v(-12.43, 78.49) * mm, "end": v(-13.45, 78.31) * mm});
            skLineSegment(sketch, "E681", {"start": v(-13.45, 78.31) * mm, "end": v(-13.58, 79.05) * mm});
            skLineSegment(sketch, "E682", {"start": v(-13.58, 79.05) * mm, "end": v(-13.93, 79) * mm});
            skLineSegment(sketch, "E683", {"start": v(-13.93, 79) * mm, "end": v(-14.27, 78.93) * mm});
            skLineSegment(sketch, "E684", {"start": v(-14.27, 78.93) * mm, "end": v(-14.14, 78.2) * mm});
            skLineSegment(sketch, "E685", {"start": v(-14.14, 78.2) * mm, "end": v(-15.16, 78) * mm});
            skLineSegment(sketch, "E686", {"start": v(-15.16, 78) * mm, "end": v(-15.4, 77.96) * mm});
            skLineSegment(sketch, "E687", {"start": v(-15.4, 77.96) * mm, "end": v(-15.55, 78.7) * mm});
            skLineSegment(sketch, "E688", {"start": v(-15.55, 78.7) * mm, "end": v(-16.24, 78.55) * mm});
            skLineSegment(sketch, "E689", {"start": v(-16.24, 78.55) * mm, "end": v(-16.09, 77.82) * mm});
            skLineSegment(sketch, "E690", {"start": v(-16.09, 77.82) * mm, "end": v(-16.52, 77.73) * mm});
            skLineSegment(sketch, "E691", {"start": v(-16.52, 77.73) * mm, "end": v(-17.34, 77.55) * mm});
            skLineSegment(sketch, "E692", {"start": v(-17.34, 77.55) * mm, "end": v(-17.5, 78.28) * mm});
            skLineSegment(sketch, "E693", {"start": v(-17.5, 78.28) * mm, "end": v(-18.04, 78.16) * mm});
            skLineSegment(sketch, "E694", {"start": v(-18.04, 78.16) * mm, "end": v(-18.2, 78.12) * mm});
            skLineSegment(sketch, "E695", {"start": v(-18.2, 78.12) * mm, "end": v(-18.02, 77.4) * mm});
            skLineSegment(sketch, "E696", {"start": v(-18.02, 77.4) * mm, "end": v(-19.27, 77.1) * mm});
            skLineSegment(sketch, "E697", {"start": v(-19.27, 77.1) * mm, "end": v(-19.45, 77.82) * mm});
            skLineSegment(sketch, "E698", {"start": v(-19.45, 77.82) * mm, "end": v(-20.13, 77.64) * mm});
            skLineSegment(sketch, "E699", {"start": v(-20.13, 77.64) * mm, "end": v(-19.95, 76.92) * mm});
            skLineSegment(sketch, "E700", {"start": v(-19.95, 76.92) * mm, "end": v(-20.57, 76.76) * mm});
            skLineSegment(sketch, "E701", {"start": v(-20.57, 76.76) * mm, "end": v(-21.18, 76.59) * mm});
            skLineSegment(sketch, "E702", {"start": v(-21.18, 76.59) * mm, "end": v(-21.39, 77.3) * mm});
            skLineSegment(sketch, "E703", {"start": v(-21.39, 77.3) * mm, "end": v(-22.06, 77.12) * mm});
            skLineSegment(sketch, "E704", {"start": v(-22.06, 77.12) * mm, "end": v(-21.86, 76.4) * mm});
            skLineSegment(sketch, "E705", {"start": v(-21.86, 76.4) * mm, "end": v(-23.09, 76.03) * mm});
            skLineSegment(sketch, "E706", {"start": v(-23.09, 76.03) * mm, "end": v(-23.3, 76.75) * mm});
            skLineSegment(sketch, "E707", {"start": v(-23.3, 76.75) * mm, "end": v(-23.45, 76.7) * mm});
            skLineSegment(sketch, "E708", {"start": v(-23.45, 76.7) * mm, "end": v(-23.98, 76.54) * mm});
            skLineSegment(sketch, "E709", {"start": v(-23.98, 76.54) * mm, "end": v(-23.76, 75.83) * mm});
            skLineSegment(sketch, "E710", {"start": v(-23.76, 75.83) * mm, "end": v(-24.56, 75.57) * mm});
            skLineSegment(sketch, "E711", {"start": v(-24.56, 75.57) * mm, "end": v(-24.98, 75.43) * mm});
            skLineSegment(sketch, "E712", {"start": v(-24.98, 75.43) * mm, "end": v(-25.21, 76.15) * mm});
            skLineSegment(sketch, "E713", {"start": v(-25.21, 76.15) * mm, "end": v(-25.88, 75.92) * mm});
            skLineSegment(sketch, "E714", {"start": v(-25.88, 75.92) * mm, "end": v(-25.64, 75.21) * mm});
            skLineSegment(sketch, "E715", {"start": v(-25.64, 75.21) * mm, "end": v(-25.87, 75.13) * mm});
            skLineSegment(sketch, "E716", {"start": v(-25.87, 75.13) * mm, "end": v(-26.85, 74.79) * mm});
            skLineSegment(sketch, "E717", {"start": v(-26.85, 74.79) * mm, "end": v(-27.1, 75.5) * mm});
            skLineSegment(sketch, "E718", {"start": v(-27.1, 75.5) * mm, "end": v(-27.43, 75.38) * mm});
            skLineSegment(sketch, "E719", {"start": v(-27.43, 75.38) * mm, "end": v(-27.76, 75.25) * mm});
            skLineSegment(sketch, "E720", {"start": v(-27.76, 75.25) * mm, "end": v(-27.5, 74.55) * mm});
            skLineSegment(sketch, "E721", {"start": v(-27.5, 74.55) * mm, "end": v(-28.48, 74.19) * mm});
            skLineSegment(sketch, "E722", {"start": v(-28.48, 74.19) * mm, "end": v(-28.7, 74.1) * mm});
            skLineSegment(sketch, "E723", {"start": v(-28.7, 74.1) * mm, "end": v(-28.98, 74.8) * mm});
            skLineSegment(sketch, "E724", {"start": v(-28.98, 74.8) * mm, "end": v(-29.63, 74.54) * mm});
            skLineSegment(sketch, "E725", {"start": v(-29.63, 74.54) * mm, "end": v(-29.36, 73.84) * mm});
            skLineSegment(sketch, "E726", {"start": v(-29.36, 73.84) * mm, "end": v(-29.77, 73.68) * mm});
            skLineSegment(sketch, "E727", {"start": v(-29.77, 73.68) * mm, "end": v(-30.54, 73.36) * mm});
            skLineSegment(sketch, "E728", {"start": v(-30.54, 73.36) * mm, "end": v(-30.83, 74.05) * mm});
            skLineSegment(sketch, "E729", {"start": v(-30.83, 74.05) * mm, "end": v(-31.34, 73.84) * mm});
            skLineSegment(sketch, "E730", {"start": v(-31.34, 73.84) * mm, "end": v(-31.48, 73.78) * mm});
            skLineSegment(sketch, "E731", {"start": v(-31.48, 73.78) * mm, "end": v(-31.19, 73.09) * mm});
            skLineSegment(sketch, "E732", {"start": v(-31.19, 73.09) * mm, "end": v(-32.36, 72.57) * mm});
            skLineSegment(sketch, "E733", {"start": v(-32.36, 72.57) * mm, "end": v(-32.67, 73.26) * mm});
            skLineSegment(sketch, "E734", {"start": v(-32.67, 73.26) * mm, "end": v(-33.3, 72.97) * mm});
            skLineSegment(sketch, "E735", {"start": v(-33.3, 72.97) * mm, "end": v(-33, 72.28) * mm});
            skLineSegment(sketch, "E736", {"start": v(-33, 72.28) * mm, "end": v(-33.58, 72.02) * mm});
            skLineSegment(sketch, "E737", {"start": v(-33.58, 72.02) * mm, "end": v(-34.16, 71.74) * mm});
            skLineSegment(sketch, "E738", {"start": v(-34.16, 71.74) * mm, "end": v(-34.49, 72.42) * mm});
            skLineSegment(sketch, "E739", {"start": v(-34.49, 72.42) * mm, "end": v(-35.12, 72.12) * mm});
            skLineSegment(sketch, "E740", {"start": v(-35.12, 72.12) * mm, "end": v(-34.8, 71.44) * mm});
            skLineSegment(sketch, "E741", {"start": v(-34.8, 71.44) * mm, "end": v(-35.94, 70.87) * mm});
            skLineSegment(sketch, "E742", {"start": v(-35.94, 70.87) * mm, "end": v(-36.28, 71.54) * mm});
            skLineSegment(sketch, "E743", {"start": v(-36.28, 71.54) * mm, "end": v(-36.42, 71.47) * mm});
            skLineSegment(sketch, "E744", {"start": v(-36.42, 71.47) * mm, "end": v(-36.9, 71.22) * mm});
            skLineSegment(sketch, "E745", {"start": v(-36.9, 71.22) * mm, "end": v(-36.56, 70.55) * mm});
            skLineSegment(sketch, "E746", {"start": v(-36.56, 70.55) * mm, "end": v(-37.3, 70.16) * mm});
            skLineSegment(sketch, "E747", {"start": v(-37.3, 70.16) * mm, "end": v(-37.7, 69.95) * mm});
            skLineSegment(sketch, "E748", {"start": v(-37.7, 69.95) * mm, "end": v(-38.05, 70.61) * mm});
            skLineSegment(sketch, "E749", {"start": v(-38.05, 70.61) * mm, "end": v(-38.67, 70.28) * mm});
            skLineSegment(sketch, "E750", {"start": v(-38.67, 70.28) * mm, "end": v(-38.31, 69.62) * mm});
            skLineSegment(sketch, "E751", {"start": v(-38.31, 69.62) * mm, "end": v(-38.52, 69.5) * mm});
            skLineSegment(sketch, "E752", {"start": v(-38.52, 69.5) * mm, "end": v(-39.43, 69) * mm});
            skLineSegment(sketch, "E753", {"start": v(-39.43, 69) * mm, "end": v(-39.8, 69.64) * mm});
            skLineSegment(sketch, "E754", {"start": v(-39.8, 69.64) * mm, "end": v(-40.1, 69.47) * mm});
            skLineSegment(sketch, "E755", {"start": v(-40.1, 69.47) * mm, "end": v(-40.4, 69.29) * mm});
            skLineSegment(sketch, "E756", {"start": v(-40.4, 69.29) * mm, "end": v(-40.03, 68.64) * mm});
            skLineSegment(sketch, "E757", {"start": v(-40.03, 68.64) * mm, "end": v(-40.93, 68.11) * mm});
            skLineSegment(sketch, "E758", {"start": v(-40.93, 68.11) * mm, "end": v(-41.14, 67.99) * mm});
            skLineSegment(sketch, "E759", {"start": v(-41.14, 67.99) * mm, "end": v(-41.53, 68.63) * mm});
            skLineSegment(sketch, "E760", {"start": v(-41.53, 68.63) * mm, "end": v(-42.12, 68.26) * mm});
            skLineSegment(sketch, "E761", {"start": v(-42.12, 68.26) * mm, "end": v(-41.73, 67.62) * mm});
            skLineSegment(sketch, "E762", {"start": v(-41.73, 67.62) * mm, "end": v(-42.1, 67.39) * mm});
            skLineSegment(sketch, "E763", {"start": v(-42.1, 67.39) * mm, "end": v(-42.82, 66.94) * mm});
            skLineSegment(sketch, "E764", {"start": v(-42.82, 66.94) * mm, "end": v(-43.22, 67.57) * mm});
            skLineSegment(sketch, "E765", {"start": v(-43.22, 67.57) * mm, "end": v(-43.69, 67.27) * mm});
            skLineSegment(sketch, "E766", {"start": v(-43.69, 67.27) * mm, "end": v(-43.81, 67.2) * mm});
            skLineSegment(sketch, "E767", {"start": v(-43.81, 67.2) * mm, "end": v(-43.4, 66.56) * mm});
            skLineSegment(sketch, "E768", {"start": v(-43.4, 66.56) * mm, "end": v(-44.47, 65.85) * mm});
            skLineSegment(sketch, "E769", {"start": v(-44.47, 65.85) * mm, "end": v(-44.9, 66.47) * mm});
            skLineSegment(sketch, "E770", {"start": v(-44.9, 66.47) * mm, "end": v(-45.47, 66.08) * mm});
            skLineSegment(sketch, "E771", {"start": v(-45.47, 66.08) * mm, "end": v(-45.05, 65.46) * mm});
            skLineSegment(sketch, "E772", {"start": v(-45.05, 65.46) * mm, "end": v(-45.58, 65.1) * mm});
            skLineSegment(sketch, "E773", {"start": v(-45.58, 65.1) * mm, "end": v(-46.1, 64.72) * mm});
            skLineSegment(sketch, "E774", {"start": v(-46.1, 64.72) * mm, "end": v(-46.54, 65.33) * mm});
            skLineSegment(sketch, "E775", {"start": v(-46.54, 65.33) * mm, "end": v(-47.1, 64.92) * mm});
            skLineSegment(sketch, "E776", {"start": v(-47.1, 64.92) * mm, "end": v(-46.67, 64.31) * mm});
            skLineSegment(sketch, "E777", {"start": v(-46.67, 64.31) * mm, "end": v(-47.7, 63.55) * mm});
            skLineSegment(sketch, "E778", {"start": v(-47.7, 63.55) * mm, "end": v(-48.15, 64.15) * mm});
            skLineSegment(sketch, "E779", {"start": v(-48.15, 64.15) * mm, "end": v(-48.27, 64.06) * mm});
            skLineSegment(sketch, "E780", {"start": v(-48.27, 64.06) * mm, "end": v(-48.71, 63.73) * mm});
            skLineSegment(sketch, "E781", {"start": v(-48.71, 63.73) * mm, "end": v(-48.26, 63.13) * mm});
            skLineSegment(sketch, "E782", {"start": v(-48.26, 63.13) * mm, "end": v(-48.92, 62.62) * mm});
            skLineSegment(sketch, "E783", {"start": v(-48.92, 62.62) * mm, "end": v(-49.27, 62.34) * mm});
            skLineSegment(sketch, "E784", {"start": v(-49.27, 62.34) * mm, "end": v(-49.74, 62.93) * mm});
            skLineSegment(sketch, "E785", {"start": v(-49.74, 62.93) * mm, "end": v(-50.28, 62.5) * mm});
            skLineSegment(sketch, "E786", {"start": v(-50.28, 62.5) * mm, "end": v(-49.82, 61.9) * mm});
            skLineSegment(sketch, "E787", {"start": v(-49.82, 61.9) * mm, "end": v(-50, 61.76) * mm});
            skLineSegment(sketch, "E788", {"start": v(-50, 61.76) * mm, "end": v(-50.8, 61.1) * mm});
            skLineSegment(sketch, "E789", {"start": v(-50.8, 61.1) * mm, "end": v(-51.3, 61.67) * mm});
            skLineSegment(sketch, "E790", {"start": v(-51.3, 61.67) * mm, "end": v(-51.56, 61.45) * mm});
            skLineSegment(sketch, "E791", {"start": v(-51.56, 61.45) * mm, "end": v(-51.83, 61.22) * mm});
            skLineSegment(sketch, "E792", {"start": v(-51.83, 61.22) * mm, "end": v(-51.34, 60.65) * mm});
            skLineSegment(sketch, "E793", {"start": v(-51.34, 60.65) * mm, "end": v(-52.13, 59.97) * mm});
            skLineSegment(sketch, "E794", {"start": v(-52.13, 59.97) * mm, "end": v(-52.32, 59.81) * mm});
            skLineSegment(sketch, "E795", {"start": v(-52.32, 59.81) * mm, "end": v(-52.81, 60.37) * mm});
            skLineSegment(sketch, "E796", {"start": v(-52.81, 60.37) * mm, "end": v(-53.34, 59.9) * mm});
            skLineSegment(sketch, "E797", {"start": v(-53.34, 59.9) * mm, "end": v(-52.84, 59.35) * mm});
            skLineSegment(sketch, "E798", {"start": v(-52.84, 59.35) * mm, "end": v(-53.17, 59.05) * mm});
            skLineSegment(sketch, "E799", {"start": v(-53.17, 59.05) * mm, "end": v(-53.8, 58.49) * mm});
            skLineSegment(sketch, "E800", {"start": v(-53.8, 58.49) * mm, "end": v(-54.3, 59.04) * mm});
            skLineSegment(sketch, "E801", {"start": v(-54.3, 59.04) * mm, "end": v(-54.7, 58.66) * mm});
            skLineSegment(sketch, "E802", {"start": v(-54.7, 58.66) * mm, "end": v(-54.81, 58.56) * mm});
            skLineSegment(sketch, "E803", {"start": v(-54.81, 58.56) * mm, "end": v(-54.3, 58.01) * mm});
            skLineSegment(sketch, "E804", {"start": v(-54.3, 58.01) * mm, "end": v(-55.23, 57.13) * mm});
            skLineSegment(sketch, "E805", {"start": v(-55.23, 57.13) * mm, "end": v(-55.76, 57.67) * mm});
            skLineSegment(sketch, "E806", {"start": v(-55.76, 57.67) * mm, "end": v(-56.26, 57.18) * mm});
            skLineSegment(sketch, "E807", {"start": v(-56.26, 57.18) * mm, "end": v(-55.73, 56.64) * mm});
            skLineSegment(sketch, "E808", {"start": v(-55.73, 56.64) * mm, "end": v(-56.19, 56.19) * mm});
            skLineSegment(sketch, "E809", {"start": v(-56.19, 56.19) * mm, "end": v(-56.64, 55.73) * mm});
            skLineSegment(sketch, "E810", {"start": v(-56.64, 55.73) * mm, "end": v(-57.18, 56.26) * mm});
            skLineSegment(sketch, "E811", {"start": v(-57.18, 56.26) * mm, "end": v(-57.67, 55.76) * mm});
            skLineSegment(sketch, "E812", {"start": v(-57.67, 55.76) * mm, "end": v(-57.13, 55.23) * mm});
            skLineSegment(sketch, "E813", {"start": v(-57.13, 55.23) * mm, "end": v(-58.01, 54.3) * mm});
            skLineSegment(sketch, "E814", {"start": v(-58.01, 54.3) * mm, "end": v(-58.56, 54.81) * mm});
            skLineSegment(sketch, "E815", {"start": v(-58.56, 54.81) * mm, "end": v(-58.66, 54.7) * mm});
            skLineSegment(sketch, "E816", {"start": v(-58.66, 54.7) * mm, "end": v(-59.04, 54.3) * mm});
            skLineSegment(sketch, "E817", {"start": v(-59.04, 54.3) * mm, "end": v(-58.49, 53.8) * mm});
            skLineSegment(sketch, "E818", {"start": v(-58.49, 53.8) * mm, "end": v(-59.05, 53.17) * mm});
            skLineSegment(sketch, "E819", {"start": v(-59.05, 53.17) * mm, "end": v(-59.35, 52.84) * mm});
            skLineSegment(sketch, "E820", {"start": v(-59.35, 52.84) * mm, "end": v(-59.9, 53.34) * mm});
            skLineSegment(sketch, "E821", {"start": v(-59.9, 53.34) * mm, "end": v(-60.37, 52.81) * mm});
            skLineSegment(sketch, "E822", {"start": v(-60.37, 52.81) * mm, "end": v(-59.81, 52.32) * mm});
            skLineSegment(sketch, "E823", {"start": v(-59.81, 52.32) * mm, "end": v(-59.97, 52.13) * mm});
            skLineSegment(sketch, "E824", {"start": v(-59.97, 52.13) * mm, "end": v(-60.65, 51.34) * mm});
            skLineSegment(sketch, "E825", {"start": v(-60.65, 51.34) * mm, "end": v(-61.22, 51.83) * mm});
            skLineSegment(sketch, "E826", {"start": v(-61.22, 51.83) * mm, "end": v(-61.45, 51.56) * mm});
            skLineSegment(sketch, "E827", {"start": v(-61.45, 51.56) * mm, "end": v(-61.67, 51.3) * mm});
            skLineSegment(sketch, "E828", {"start": v(-61.67, 51.3) * mm, "end": v(-61.1, 50.8) * mm});
            skLineSegment(sketch, "E829", {"start": v(-61.1, 50.8) * mm, "end": v(-61.76, 50) * mm});
            skLineSegment(sketch, "E830", {"start": v(-61.76, 50) * mm, "end": v(-61.9, 49.82) * mm});
            skLineSegment(sketch, "E831", {"start": v(-61.9, 49.82) * mm, "end": v(-62.5, 50.28) * mm});
            skLineSegment(sketch, "E832", {"start": v(-62.5, 50.28) * mm, "end": v(-62.93, 49.74) * mm});
            skLineSegment(sketch, "E833", {"start": v(-62.93, 49.74) * mm, "end": v(-62.34, 49.27) * mm});
            skLineSegment(sketch, "E834", {"start": v(-62.34, 49.27) * mm, "end": v(-62.62, 48.92) * mm});
            skLineSegment(sketch, "E835", {"start": v(-62.62, 48.92) * mm, "end": v(-63.13, 48.26) * mm});
            skLineSegment(sketch, "E836", {"start": v(-63.13, 48.26) * mm, "end": v(-63.73, 48.71) * mm});
            skLineSegment(sketch, "E837", {"start": v(-63.73, 48.71) * mm, "end": v(-64.06, 48.27) * mm});
            skLineSegment(sketch, "E838", {"start": v(-64.06, 48.27) * mm, "end": v(-64.15, 48.15) * mm});
            skLineSegment(sketch, "E839", {"start": v(-64.15, 48.15) * mm, "end": v(-63.55, 47.7) * mm});
            skLineSegment(sketch, "E840", {"start": v(-63.55, 47.7) * mm, "end": v(-64.31, 46.67) * mm});
            skLineSegment(sketch, "E841", {"start": v(-64.31, 46.67) * mm, "end": v(-64.92, 47.1) * mm});
            skLineSegment(sketch, "E842", {"start": v(-64.92, 47.1) * mm, "end": v(-65.33, 46.54) * mm});
            skLineSegment(sketch, "E843", {"start": v(-65.33, 46.54) * mm, "end": v(-64.72, 46.1) * mm});
            skLineSegment(sketch, "E844", {"start": v(-64.72, 46.1) * mm, "end": v(-65.1, 45.58) * mm});
            skLineSegment(sketch, "E845", {"start": v(-65.1, 45.58) * mm, "end": v(-65.46, 45.05) * mm});
            skLineSegment(sketch, "E846", {"start": v(-65.46, 45.05) * mm, "end": v(-66.08, 45.47) * mm});
            skLineSegment(sketch, "E847", {"start": v(-66.08, 45.47) * mm, "end": v(-66.47, 44.9) * mm});
            skLineSegment(sketch, "E848", {"start": v(-66.47, 44.9) * mm, "end": v(-65.85, 44.47) * mm});
            skLineSegment(sketch, "E849", {"start": v(-65.85, 44.47) * mm, "end": v(-66.56, 43.4) * mm});
            skLineSegment(sketch, "E850", {"start": v(-66.56, 43.4) * mm, "end": v(-67.2, 43.81) * mm});
            skLineSegment(sketch, "E851", {"start": v(-67.2, 43.81) * mm, "end": v(-67.27, 43.69) * mm});
            skLineSegment(sketch, "E852", {"start": v(-67.27, 43.69) * mm, "end": v(-67.57, 43.22) * mm});
            skLineSegment(sketch, "E853", {"start": v(-67.57, 43.22) * mm, "end": v(-66.94, 42.82) * mm});
            skLineSegment(sketch, "E854", {"start": v(-66.94, 42.82) * mm, "end": v(-67.39, 42.1) * mm});
            skLineSegment(sketch, "E855", {"start": v(-67.39, 42.1) * mm, "end": v(-67.62, 41.73) * mm});
            skLineSegment(sketch, "E856", {"start": v(-67.62, 41.73) * mm, "end": v(-68.26, 42.12) * mm});
            skLineSegment(sketch, "E857", {"start": v(-68.26, 42.12) * mm, "end": v(-68.63, 41.53) * mm});
            skLineSegment(sketch, "E858", {"start": v(-68.63, 41.53) * mm, "end": v(-67.99, 41.14) * mm});
            skLineSegment(sketch, "E859", {"start": v(-67.99, 41.14) * mm, "end": v(-68.11, 40.93) * mm});
            skLineSegment(sketch, "E860", {"start": v(-68.11, 40.93) * mm, "end": v(-68.64, 40.03) * mm});
            skLineSegment(sketch, "E861", {"start": v(-68.64, 40.03) * mm, "end": v(-69.29, 40.4) * mm});
            skLineSegment(sketch, "E862", {"start": v(-69.29, 40.4) * mm, "end": v(-69.47, 40.1) * mm});
            skLineSegment(sketch, "E863", {"start": v(-69.47, 40.1) * mm, "end": v(-69.64, 39.8) * mm});
            skLineSegment(sketch, "E864", {"start": v(-69.64, 39.8) * mm, "end": v(-69, 39.43) * mm});
            skLineSegment(sketch, "E865", {"start": v(-69, 39.43) * mm, "end": v(-69.5, 38.52) * mm});
            skLineSegment(sketch, "E866", {"start": v(-69.5, 38.52) * mm, "end": v(-69.62, 38.31) * mm});
            skLineSegment(sketch, "E867", {"start": v(-69.62, 38.31) * mm, "end": v(-70.28, 38.67) * mm});
            skLineSegment(sketch, "E868", {"start": v(-70.28, 38.67) * mm, "end": v(-70.61, 38.05) * mm});
            skLineSegment(sketch, "E869", {"start": v(-70.61, 38.05) * mm, "end": v(-69.95, 37.7) * mm});
            skLineSegment(sketch, "E870", {"start": v(-69.95, 37.7) * mm, "end": v(-70.16, 37.3) * mm});
            skLineSegment(sketch, "E871", {"start": v(-70.16, 37.3) * mm, "end": v(-70.55, 36.56) * mm});
            skLineSegment(sketch, "E872", {"start": v(-70.55, 36.56) * mm, "end": v(-71.22, 36.9) * mm});
            skLineSegment(sketch, "E873", {"start": v(-71.22, 36.9) * mm, "end": v(-71.47, 36.42) * mm});
            skLineSegment(sketch, "E874", {"start": v(-71.47, 36.42) * mm, "end": v(-71.54, 36.28) * mm});
            skLineSegment(sketch, "E875", {"start": v(-71.54, 36.28) * mm, "end": v(-70.87, 35.94) * mm});
            skLineSegment(sketch, "E876", {"start": v(-70.87, 35.94) * mm, "end": v(-71.44, 34.8) * mm});
            skLineSegment(sketch, "E877", {"start": v(-71.44, 34.8) * mm, "end": v(-72.12, 35.12) * mm});
            skLineSegment(sketch, "E878", {"start": v(-72.12, 35.12) * mm, "end": v(-72.42, 34.49) * mm});
            skLineSegment(sketch, "E879", {"start": v(-72.42, 34.49) * mm, "end": v(-71.74, 34.16) * mm});
            skLineSegment(sketch, "E880", {"start": v(-71.74, 34.16) * mm, "end": v(-72.02, 33.58) * mm});
            skLineSegment(sketch, "E881", {"start": v(-72.02, 33.58) * mm, "end": v(-72.28, 33) * mm});
            skLineSegment(sketch, "E882", {"start": v(-72.28, 33) * mm, "end": v(-72.97, 33.3) * mm});
            skLineSegment(sketch, "E883", {"start": v(-72.97, 33.3) * mm, "end": v(-73.26, 32.67) * mm});
            skLineSegment(sketch, "E884", {"start": v(-73.26, 32.67) * mm, "end": v(-72.57, 32.36) * mm});
            skLineSegment(sketch, "E885", {"start": v(-72.57, 32.36) * mm, "end": v(-73.09, 31.19) * mm});
            skLineSegment(sketch, "E886", {"start": v(-73.09, 31.19) * mm, "end": v(-73.78, 31.48) * mm});
            skLineSegment(sketch, "E887", {"start": v(-73.78, 31.48) * mm, "end": v(-73.84, 31.34) * mm});
            skLineSegment(sketch, "E888", {"start": v(-73.84, 31.34) * mm, "end": v(-74.05, 30.83) * mm});
            skLineSegment(sketch, "E889", {"start": v(-74.05, 30.83) * mm, "end": v(-73.36, 30.54) * mm});
            skLineSegment(sketch, "E890", {"start": v(-73.36, 30.54) * mm, "end": v(-73.68, 29.77) * mm});
            skLineSegment(sketch, "E891", {"start": v(-73.68, 29.77) * mm, "end": v(-73.84, 29.36) * mm});
            skLineSegment(sketch, "E892", {"start": v(-73.84, 29.36) * mm, "end": v(-74.54, 29.63) * mm});
            skLineSegment(sketch, "E893", {"start": v(-74.54, 29.63) * mm, "end": v(-74.8, 28.98) * mm});
            skLineSegment(sketch, "E894", {"start": v(-74.8, 28.98) * mm, "end": v(-74.1, 28.7) * mm});
            skLineSegment(sketch, "E895", {"start": v(-74.1, 28.7) * mm, "end": v(-74.19, 28.48) * mm});
            skLineSegment(sketch, "E896", {"start": v(-74.19, 28.48) * mm, "end": v(-74.55, 27.5) * mm});
            skLineSegment(sketch, "E897", {"start": v(-74.55, 27.5) * mm, "end": v(-75.25, 27.76) * mm});
            skLineSegment(sketch, "E898", {"start": v(-75.25, 27.76) * mm, "end": v(-75.38, 27.43) * mm});
            skLineSegment(sketch, "E899", {"start": v(-75.38, 27.43) * mm, "end": v(-75.5, 27.1) * mm});
            skLineSegment(sketch, "E900", {"start": v(-75.5, 27.1) * mm, "end": v(-74.79, 26.85) * mm});
            skLineSegment(sketch, "E901", {"start": v(-74.79, 26.85) * mm, "end": v(-75.13, 25.87) * mm});
            skLineSegment(sketch, "E902", {"start": v(-75.13, 25.87) * mm, "end": v(-75.21, 25.64) * mm});
            skLineSegment(sketch, "E903", {"start": v(-75.21, 25.64) * mm, "end": v(-75.92, 25.88) * mm});
            skLineSegment(sketch, "E904", {"start": v(-75.92, 25.88) * mm, "end": v(-76.15, 25.21) * mm});
            skLineSegment(sketch, "E905", {"start": v(-76.15, 25.21) * mm, "end": v(-75.43, 24.98) * mm});
            skLineSegment(sketch, "E906", {"start": v(-75.43, 24.98) * mm, "end": v(-75.57, 24.56) * mm});
            skLineSegment(sketch, "E907", {"start": v(-75.57, 24.56) * mm, "end": v(-75.83, 23.76) * mm});
            skLineSegment(sketch, "E908", {"start": v(-75.83, 23.76) * mm, "end": v(-76.54, 23.98) * mm});
            skLineSegment(sketch, "E909", {"start": v(-76.54, 23.98) * mm, "end": v(-76.7, 23.45) * mm});
            skLineSegment(sketch, "E910", {"start": v(-76.7, 23.45) * mm, "end": v(-76.75, 23.3) * mm});
            skLineSegment(sketch, "E911", {"start": v(-76.75, 23.3) * mm, "end": v(-76.03, 23.09) * mm});
            skLineSegment(sketch, "E912", {"start": v(-76.03, 23.09) * mm, "end": v(-76.4, 21.86) * mm});
            skLineSegment(sketch, "E913", {"start": v(-76.4, 21.86) * mm, "end": v(-77.12, 22.06) * mm});
            skLineSegment(sketch, "E914", {"start": v(-77.12, 22.06) * mm, "end": v(-77.3, 21.39) * mm});
            skLineSegment(sketch, "E915", {"start": v(-77.3, 21.39) * mm, "end": v(-76.59, 21.18) * mm});
            skLineSegment(sketch, "E916", {"start": v(-76.59, 21.18) * mm, "end": v(-76.76, 20.57) * mm});
            skLineSegment(sketch, "E917", {"start": v(-76.76, 20.57) * mm, "end": v(-76.92, 19.95) * mm});
            skLineSegment(sketch, "E918", {"start": v(-76.92, 19.95) * mm, "end": v(-77.64, 20.13) * mm});
            skLineSegment(sketch, "E919", {"start": v(-77.64, 20.13) * mm, "end": v(-77.82, 19.45) * mm});
            skLineSegment(sketch, "E920", {"start": v(-77.82, 19.45) * mm, "end": v(-77.1, 19.27) * mm});
            skLineSegment(sketch, "E921", {"start": v(-77.1, 19.27) * mm, "end": v(-77.4, 18.02) * mm});
            skLineSegment(sketch, "E922", {"start": v(-77.4, 18.02) * mm, "end": v(-78.12, 18.2) * mm});
            skLineSegment(sketch, "E923", {"start": v(-78.12, 18.2) * mm, "end": v(-78.16, 18.04) * mm});
            skLineSegment(sketch, "E924", {"start": v(-78.16, 18.04) * mm, "end": v(-78.28, 17.5) * mm});
            skLineSegment(sketch, "E925", {"start": v(-78.28, 17.5) * mm, "end": v(-77.55, 17.34) * mm});
            skLineSegment(sketch, "E926", {"start": v(-77.55, 17.34) * mm, "end": v(-77.73, 16.52) * mm});
            skLineSegment(sketch, "E927", {"start": v(-77.73, 16.52) * mm, "end": v(-77.82, 16.09) * mm});
            skLineSegment(sketch, "E928", {"start": v(-77.82, 16.09) * mm, "end": v(-78.55, 16.24) * mm});
            skLineSegment(sketch, "E929", {"start": v(-78.55, 16.24) * mm, "end": v(-78.7, 15.55) * mm});
            skLineSegment(sketch, "E930", {"start": v(-78.7, 15.55) * mm, "end": v(-77.96, 15.4) * mm});
            skLineSegment(sketch, "E931", {"start": v(-77.96, 15.4) * mm, "end": v(-78, 15.16) * mm});
            skLineSegment(sketch, "E932", {"start": v(-78, 15.16) * mm, "end": v(-78.2, 14.14) * mm});
            skLineSegment(sketch, "E933", {"start": v(-78.2, 14.14) * mm, "end": v(-78.93, 14.27) * mm});
            skLineSegment(sketch, "E934", {"start": v(-78.93, 14.27) * mm, "end": v(-79, 13.93) * mm});
            skLineSegment(sketch, "E935", {"start": v(-79, 13.93) * mm, "end": v(-79.05, 13.58) * mm});
            skLineSegment(sketch, "E936", {"start": v(-79.05, 13.58) * mm, "end": v(-78.31, 13.45) * mm});
            skLineSegment(sketch, "E937", {"start": v(-78.31, 13.45) * mm, "end": v(-78.49, 12.43) * mm});
            skLineSegment(sketch, "E938", {"start": v(-78.49, 12.43) * mm, "end": v(-78.52, 12.19) * mm});
            skLineSegment(sketch, "E939", {"start": v(-78.52, 12.19) * mm, "end": v(-79.26, 12.3) * mm});
            skLineSegment(sketch, "E940", {"start": v(-79.26, 12.3) * mm, "end": v(-79.37, 11.6) * mm});
            skLineSegment(sketch, "E941", {"start": v(-79.37, 11.6) * mm, "end": v(-78.63, 11.5) * mm});
            skLineSegment(sketch, "E942", {"start": v(-78.63, 11.5) * mm, "end": v(-78.7, 11.06) * mm});
            skLineSegment(sketch, "E943", {"start": v(-78.7, 11.06) * mm, "end": v(-78.8, 10.23) * mm});
            skLineSegment(sketch, "E944", {"start": v(-78.8, 10.23) * mm, "end": v(-79.54, 10.32) * mm});
            skLineSegment(sketch, "E945", {"start": v(-79.54, 10.32) * mm, "end": v(-79.62, 9.78) * mm});
            skLineSegment(sketch, "E946", {"start": v(-79.62, 9.78) * mm, "end": v(-79.63, 9.63) * mm});
            skLineSegment(sketch, "E947", {"start": v(-79.63, 9.63) * mm, "end": v(-78.89, 9.53) * mm});
            skLineSegment(sketch, "E948", {"start": v(-78.89, 9.53) * mm, "end": v(-79.03, 8.26) * mm});
            skLineSegment(sketch, "E949", {"start": v(-79.03, 8.26) * mm, "end": v(-79.78, 8.33) * mm});
            skLineSegment(sketch, "E950", {"start": v(-79.78, 8.33) * mm, "end": v(-79.85, 7.64) * mm});
            skLineSegment(sketch, "E951", {"start": v(-79.85, 7.64) * mm, "end": v(-79.1, 7.56) * mm});
            skLineSegment(sketch, "E952", {"start": v(-79.1, 7.56) * mm, "end": v(-79.16, 6.93) * mm});
            skLineSegment(sketch, "E953", {"start": v(-79.16, 6.93) * mm, "end": v(-79.21, 6.29) * mm});
            skLineSegment(sketch, "E954", {"start": v(-79.21, 6.29) * mm, "end": v(-79.96, 6.34) * mm});
            skLineSegment(sketch, "E955", {"start": v(-79.96, 6.34) * mm, "end": v(-80.01, 5.65) * mm});
            skLineSegment(sketch, "E956", {"start": v(-80.01, 5.65) * mm, "end": v(-79.27, 5.59) * mm});
            skLineSegment(sketch, "E957", {"start": v(-79.27, 5.59) * mm, "end": v(-79.35, 4.31) * mm});
            skLineSegment(sketch, "E958", {"start": v(-79.35, 4.31) * mm, "end": v(-80.1, 4.35) * mm});
            skLineSegment(sketch, "E959", {"start": v(-80.1, 4.35) * mm, "end": v(-80.1, 4.2) * mm});
            skLineSegment(sketch, "E960", {"start": v(-80.1, 4.2) * mm, "end": v(-80.13, 3.65) * mm});
            skLineSegment(sketch, "E961", {"start": v(-80.13, 3.65) * mm, "end": v(-79.38, 3.61) * mm});
            skLineSegment(sketch, "E962", {"start": v(-79.38, 3.61) * mm, "end": v(-79.42, 2.77) * mm});
            skLineSegment(sketch, "E963", {"start": v(-79.42, 2.77) * mm, "end": v(-79.43, 2.33) * mm});
            skLineSegment(sketch, "E964", {"start": v(-79.43, 2.33) * mm, "end": v(-80.18, 2.35) * mm});
            skLineSegment(sketch, "E965", {"start": v(-80.18, 2.35) * mm, "end": v(-80.2, 1.65) * mm});
            skLineSegment(sketch, "E966", {"start": v(-80.2, 1.65) * mm, "end": v(-79.45, 1.63) * mm});
            skLineSegment(sketch, "E967", {"start": v(-79.45, 1.63) * mm, "end": v(-79.45, 1.39) * mm});
            skLineSegment(sketch, "E968", {"start": v(-79.45, 1.39) * mm, "end": v(-79.46, 0.35) * mm});
            skLineSegment(sketch, "E969", {"start": v(-79.46, 0.35) * mm, "end": v(-80.21, 0.35) * mm});
            skLineSegment(sketch, "E970", {"start": v(-80.21, 0.35) * mm, "end": v(-80.21, 0) * mm});
            skLineSegment(sketch, "E971", {"start": v(-80.21, 0) * mm, "end": v(-80.21, -0.35) * mm});
            skLineSegment(sketch, "E972", {"start": v(-80.21, -0.35) * mm, "end": v(-79.46, -0.35) * mm});
            skLineSegment(sketch, "E973", {"start": v(-79.46, -0.35) * mm, "end": v(-79.45, -1.39) * mm});
            skLineSegment(sketch, "E974", {"start": v(-79.45, -1.39) * mm, "end": v(-79.45, -1.63) * mm});
            skLineSegment(sketch, "E975", {"start": v(-79.45, -1.63) * mm, "end": v(-80.2, -1.65) * mm});
            skLineSegment(sketch, "E976", {"start": v(-80.2, -1.65) * mm, "end": v(-80.18, -2.35) * mm});
            skLineSegment(sketch, "E977", {"start": v(-80.18, -2.35) * mm, "end": v(-79.43, -2.33) * mm});
            skLineSegment(sketch, "E978", {"start": v(-79.43, -2.33) * mm, "end": v(-79.42, -2.77) * mm});
            skLineSegment(sketch, "E979", {"start": v(-79.42, -2.77) * mm, "end": v(-79.38, -3.61) * mm});
            skLineSegment(sketch, "E980", {"start": v(-79.38, -3.61) * mm, "end": v(-80.13, -3.65) * mm});
            skLineSegment(sketch, "E981", {"start": v(-80.13, -3.65) * mm, "end": v(-80.1, -4.2) * mm});
            skLineSegment(sketch, "E982", {"start": v(-80.1, -4.2) * mm, "end": v(-80.1, -4.35) * mm});
            skLineSegment(sketch, "E983", {"start": v(-80.1, -4.35) * mm, "end": v(-79.35, -4.31) * mm});
            skLineSegment(sketch, "E984", {"start": v(-79.35, -4.31) * mm, "end": v(-79.27, -5.59) * mm});
            skLineSegment(sketch, "E985", {"start": v(-79.27, -5.59) * mm, "end": v(-80.01, -5.65) * mm});
            skLineSegment(sketch, "E986", {"start": v(-80.01, -5.65) * mm, "end": v(-79.96, -6.34) * mm});
            skLineSegment(sketch, "E987", {"start": v(-79.96, -6.34) * mm, "end": v(-79.21, -6.29) * mm});
            skLineSegment(sketch, "E988", {"start": v(-79.21, -6.29) * mm, "end": v(-79.16, -6.93) * mm});
            skLineSegment(sketch, "E989", {"start": v(-79.16, -6.93) * mm, "end": v(-79.1, -7.56) * mm});
            skLineSegment(sketch, "E990", {"start": v(-79.1, -7.56) * mm, "end": v(-79.85, -7.64) * mm});
            skLineSegment(sketch, "E991", {"start": v(-79.85, -7.64) * mm, "end": v(-79.78, -8.33) * mm});
            skLineSegment(sketch, "E992", {"start": v(-79.78, -8.33) * mm, "end": v(-79.03, -8.26) * mm});
            skLineSegment(sketch, "E993", {"start": v(-79.03, -8.26) * mm, "end": v(-78.89, -9.53) * mm});
            skLineSegment(sketch, "E994", {"start": v(-78.89, -9.53) * mm, "end": v(-79.63, -9.63) * mm});
            skLineSegment(sketch, "E995", {"start": v(-79.63, -9.63) * mm, "end": v(-79.62, -9.78) * mm});
            skLineSegment(sketch, "E996", {"start": v(-79.62, -9.78) * mm, "end": v(-79.54, -10.32) * mm});
            skLineSegment(sketch, "E997", {"start": v(-79.54, -10.32) * mm, "end": v(-78.8, -10.23) * mm});
            skLineSegment(sketch, "E998", {"start": v(-78.8, -10.23) * mm, "end": v(-78.7, -11.06) * mm});
            skLineSegment(sketch, "E999", {"start": v(-78.7, -11.06) * mm, "end": v(-78.63, -11.5) * mm});
            skLineSegment(sketch, "E1000", {"start": v(-78.63, -11.5) * mm, "end": v(-79.37, -11.6) * mm});
            skLineSegment(sketch, "E1001", {"start": v(-79.37, -11.6) * mm, "end": v(-79.26, -12.3) * mm});
            skLineSegment(sketch, "E1002", {"start": v(-79.26, -12.3) * mm, "end": v(-78.52, -12.19) * mm});
            skLineSegment(sketch, "E1003", {"start": v(-78.52, -12.19) * mm, "end": v(-78.49, -12.43) * mm});
            skLineSegment(sketch, "E1004", {"start": v(-78.49, -12.43) * mm, "end": v(-78.31, -13.45) * mm});
            skLineSegment(sketch, "E1005", {"start": v(-78.31, -13.45) * mm, "end": v(-79.05, -13.58) * mm});
            skLineSegment(sketch, "E1006", {"start": v(-79.05, -13.58) * mm, "end": v(-79, -13.93) * mm});
            skLineSegment(sketch, "E1007", {"start": v(-79, -13.93) * mm, "end": v(-78.93, -14.27) * mm});
            skLineSegment(sketch, "E1008", {"start": v(-78.93, -14.27) * mm, "end": v(-78.2, -14.14) * mm});
            skLineSegment(sketch, "E1009", {"start": v(-78.2, -14.14) * mm, "end": v(-78, -15.16) * mm});
            skLineSegment(sketch, "E1010", {"start": v(-78, -15.16) * mm, "end": v(-77.96, -15.4) * mm});
            skLineSegment(sketch, "E1011", {"start": v(-77.96, -15.4) * mm, "end": v(-78.7, -15.55) * mm});
            skLineSegment(sketch, "E1012", {"start": v(-78.7, -15.55) * mm, "end": v(-78.55, -16.24) * mm});
            skLineSegment(sketch, "E1013", {"start": v(-78.55, -16.24) * mm, "end": v(-77.82, -16.09) * mm});
            skLineSegment(sketch, "E1014", {"start": v(-77.82, -16.09) * mm, "end": v(-77.73, -16.52) * mm});
            skLineSegment(sketch, "E1015", {"start": v(-77.73, -16.52) * mm, "end": v(-77.55, -17.34) * mm});
            skLineSegment(sketch, "E1016", {"start": v(-77.55, -17.34) * mm, "end": v(-78.28, -17.5) * mm});
            skLineSegment(sketch, "E1017", {"start": v(-78.28, -17.5) * mm, "end": v(-78.16, -18.04) * mm});
            skLineSegment(sketch, "E1018", {"start": v(-78.16, -18.04) * mm, "end": v(-78.12, -18.2) * mm});
            skLineSegment(sketch, "E1019", {"start": v(-78.12, -18.2) * mm, "end": v(-77.4, -18.02) * mm});
            skLineSegment(sketch, "E1020", {"start": v(-77.4, -18.02) * mm, "end": v(-77.1, -19.27) * mm});
            skLineSegment(sketch, "E1021", {"start": v(-77.1, -19.27) * mm, "end": v(-77.82, -19.45) * mm});
            skLineSegment(sketch, "E1022", {"start": v(-77.82, -19.45) * mm, "end": v(-77.64, -20.13) * mm});
            skLineSegment(sketch, "E1023", {"start": v(-77.64, -20.13) * mm, "end": v(-76.92, -19.95) * mm});
            skLineSegment(sketch, "E1024", {"start": v(-76.92, -19.95) * mm, "end": v(-76.76, -20.57) * mm});
            skLineSegment(sketch, "E1025", {"start": v(-76.76, -20.57) * mm, "end": v(-76.59, -21.18) * mm});
            skLineSegment(sketch, "E1026", {"start": v(-76.59, -21.18) * mm, "end": v(-77.3, -21.39) * mm});
            skLineSegment(sketch, "E1027", {"start": v(-77.3, -21.39) * mm, "end": v(-77.12, -22.06) * mm});
            skLineSegment(sketch, "E1028", {"start": v(-77.12, -22.06) * mm, "end": v(-76.4, -21.86) * mm});
            skLineSegment(sketch, "E1029", {"start": v(-76.4, -21.86) * mm, "end": v(-76.03, -23.09) * mm});
            skLineSegment(sketch, "E1030", {"start": v(-76.03, -23.09) * mm, "end": v(-76.75, -23.3) * mm});
            skLineSegment(sketch, "E1031", {"start": v(-76.75, -23.3) * mm, "end": v(-76.7, -23.45) * mm});
            skLineSegment(sketch, "E1032", {"start": v(-76.7, -23.45) * mm, "end": v(-76.54, -23.98) * mm});
            skLineSegment(sketch, "E1033", {"start": v(-76.54, -23.98) * mm, "end": v(-75.83, -23.76) * mm});
            skLineSegment(sketch, "E1034", {"start": v(-75.83, -23.76) * mm, "end": v(-75.57, -24.56) * mm});
            skLineSegment(sketch, "E1035", {"start": v(-75.57, -24.56) * mm, "end": v(-75.43, -24.98) * mm});
            skLineSegment(sketch, "E1036", {"start": v(-75.43, -24.98) * mm, "end": v(-76.15, -25.21) * mm});
            skLineSegment(sketch, "E1037", {"start": v(-76.15, -25.21) * mm, "end": v(-75.92, -25.88) * mm});
            skLineSegment(sketch, "E1038", {"start": v(-75.92, -25.88) * mm, "end": v(-75.21, -25.64) * mm});
            skLineSegment(sketch, "E1039", {"start": v(-75.21, -25.64) * mm, "end": v(-75.13, -25.87) * mm});
            skLineSegment(sketch, "E1040", {"start": v(-75.13, -25.87) * mm, "end": v(-74.79, -26.85) * mm});
            skLineSegment(sketch, "E1041", {"start": v(-74.79, -26.85) * mm, "end": v(-75.5, -27.1) * mm});
            skLineSegment(sketch, "E1042", {"start": v(-75.5, -27.1) * mm, "end": v(-75.38, -27.43) * mm});
            skLineSegment(sketch, "E1043", {"start": v(-75.38, -27.43) * mm, "end": v(-75.25, -27.76) * mm});
            skLineSegment(sketch, "E1044", {"start": v(-75.25, -27.76) * mm, "end": v(-74.55, -27.5) * mm});
            skLineSegment(sketch, "E1045", {"start": v(-74.55, -27.5) * mm, "end": v(-74.19, -28.48) * mm});
            skLineSegment(sketch, "E1046", {"start": v(-74.19, -28.48) * mm, "end": v(-74.1, -28.7) * mm});
            skLineSegment(sketch, "E1047", {"start": v(-74.1, -28.7) * mm, "end": v(-74.8, -28.98) * mm});
            skLineSegment(sketch, "E1048", {"start": v(-74.8, -28.98) * mm, "end": v(-74.54, -29.63) * mm});
            skLineSegment(sketch, "E1049", {"start": v(-74.54, -29.63) * mm, "end": v(-73.84, -29.36) * mm});
            skLineSegment(sketch, "E1050", {"start": v(-73.84, -29.36) * mm, "end": v(-73.68, -29.77) * mm});
            skLineSegment(sketch, "E1051", {"start": v(-73.68, -29.77) * mm, "end": v(-73.36, -30.54) * mm});
            skLineSegment(sketch, "E1052", {"start": v(-73.36, -30.54) * mm, "end": v(-74.05, -30.83) * mm});
            skLineSegment(sketch, "E1053", {"start": v(-74.05, -30.83) * mm, "end": v(-73.84, -31.34) * mm});
            skLineSegment(sketch, "E1054", {"start": v(-73.84, -31.34) * mm, "end": v(-73.78, -31.48) * mm});
            skLineSegment(sketch, "E1055", {"start": v(-73.78, -31.48) * mm, "end": v(-73.09, -31.19) * mm});
            skLineSegment(sketch, "E1056", {"start": v(-73.09, -31.19) * mm, "end": v(-72.57, -32.36) * mm});
            skLineSegment(sketch, "E1057", {"start": v(-72.57, -32.36) * mm, "end": v(-73.26, -32.67) * mm});
            skLineSegment(sketch, "E1058", {"start": v(-73.26, -32.67) * mm, "end": v(-72.97, -33.3) * mm});
            skLineSegment(sketch, "E1059", {"start": v(-72.97, -33.3) * mm, "end": v(-72.28, -33) * mm});
            skLineSegment(sketch, "E1060", {"start": v(-72.28, -33) * mm, "end": v(-72.02, -33.58) * mm});
            skLineSegment(sketch, "E1061", {"start": v(-72.02, -33.58) * mm, "end": v(-71.74, -34.16) * mm});
            skLineSegment(sketch, "E1062", {"start": v(-71.74, -34.16) * mm, "end": v(-72.42, -34.49) * mm});
            skLineSegment(sketch, "E1063", {"start": v(-72.42, -34.49) * mm, "end": v(-72.12, -35.12) * mm});
            skLineSegment(sketch, "E1064", {"start": v(-72.12, -35.12) * mm, "end": v(-71.44, -34.8) * mm});
            skLineSegment(sketch, "E1065", {"start": v(-71.44, -34.8) * mm, "end": v(-70.87, -35.94) * mm});
            skLineSegment(sketch, "E1066", {"start": v(-70.87, -35.94) * mm, "end": v(-71.54, -36.28) * mm});
            skLineSegment(sketch, "E1067", {"start": v(-71.54, -36.28) * mm, "end": v(-71.47, -36.42) * mm});
            skLineSegment(sketch, "E1068", {"start": v(-71.47, -36.42) * mm, "end": v(-71.22, -36.9) * mm});
            skLineSegment(sketch, "E1069", {"start": v(-71.22, -36.9) * mm, "end": v(-70.55, -36.56) * mm});
            skLineSegment(sketch, "E1070", {"start": v(-70.55, -36.56) * mm, "end": v(-70.16, -37.3) * mm});
            skLineSegment(sketch, "E1071", {"start": v(-70.16, -37.3) * mm, "end": v(-69.95, -37.7) * mm});
            skLineSegment(sketch, "E1072", {"start": v(-69.95, -37.7) * mm, "end": v(-70.61, -38.05) * mm});
            skLineSegment(sketch, "E1073", {"start": v(-70.61, -38.05) * mm, "end": v(-70.28, -38.67) * mm});
            skLineSegment(sketch, "E1074", {"start": v(-70.28, -38.67) * mm, "end": v(-69.62, -38.31) * mm});
            skLineSegment(sketch, "E1075", {"start": v(-69.62, -38.31) * mm, "end": v(-69.5, -38.52) * mm});
            skLineSegment(sketch, "E1076", {"start": v(-69.5, -38.52) * mm, "end": v(-69, -39.43) * mm});
            skLineSegment(sketch, "E1077", {"start": v(-69, -39.43) * mm, "end": v(-69.64, -39.8) * mm});
            skLineSegment(sketch, "E1078", {"start": v(-69.64, -39.8) * mm, "end": v(-69.47, -40.1) * mm});
            skLineSegment(sketch, "E1079", {"start": v(-69.47, -40.1) * mm, "end": v(-69.29, -40.4) * mm});
            skLineSegment(sketch, "E1080", {"start": v(-69.29, -40.4) * mm, "end": v(-68.64, -40.03) * mm});
            skLineSegment(sketch, "E1081", {"start": v(-68.64, -40.03) * mm, "end": v(-68.11, -40.93) * mm});
            skLineSegment(sketch, "E1082", {"start": v(-68.11, -40.93) * mm, "end": v(-67.99, -41.14) * mm});
            skLineSegment(sketch, "E1083", {"start": v(-67.99, -41.14) * mm, "end": v(-68.63, -41.53) * mm});
            skLineSegment(sketch, "E1084", {"start": v(-68.63, -41.53) * mm, "end": v(-68.26, -42.12) * mm});
            skLineSegment(sketch, "E1085", {"start": v(-68.26, -42.12) * mm, "end": v(-67.62, -41.73) * mm});
            skLineSegment(sketch, "E1086", {"start": v(-67.62, -41.73) * mm, "end": v(-67.39, -42.1) * mm});
            skLineSegment(sketch, "E1087", {"start": v(-67.39, -42.1) * mm, "end": v(-66.94, -42.82) * mm});
            skLineSegment(sketch, "E1088", {"start": v(-66.94, -42.82) * mm, "end": v(-67.57, -43.22) * mm});
            skLineSegment(sketch, "E1089", {"start": v(-67.57, -43.22) * mm, "end": v(-67.27, -43.69) * mm});
            skLineSegment(sketch, "E1090", {"start": v(-67.27, -43.69) * mm, "end": v(-67.2, -43.81) * mm});
            skLineSegment(sketch, "E1091", {"start": v(-67.2, -43.81) * mm, "end": v(-66.56, -43.4) * mm});
            skLineSegment(sketch, "E1092", {"start": v(-66.56, -43.4) * mm, "end": v(-65.85, -44.47) * mm});
            skLineSegment(sketch, "E1093", {"start": v(-65.85, -44.47) * mm, "end": v(-66.47, -44.9) * mm});
            skLineSegment(sketch, "E1094", {"start": v(-66.47, -44.9) * mm, "end": v(-66.08, -45.47) * mm});
            skLineSegment(sketch, "E1095", {"start": v(-66.08, -45.47) * mm, "end": v(-65.46, -45.05) * mm});
            skLineSegment(sketch, "E1096", {"start": v(-65.46, -45.05) * mm, "end": v(-65.1, -45.58) * mm});
            skLineSegment(sketch, "E1097", {"start": v(-65.1, -45.58) * mm, "end": v(-64.72, -46.1) * mm});
            skLineSegment(sketch, "E1098", {"start": v(-64.72, -46.1) * mm, "end": v(-65.33, -46.54) * mm});
            skLineSegment(sketch, "E1099", {"start": v(-65.33, -46.54) * mm, "end": v(-64.92, -47.1) * mm});
            skLineSegment(sketch, "E1100", {"start": v(-64.92, -47.1) * mm, "end": v(-64.31, -46.67) * mm});
            skLineSegment(sketch, "E1101", {"start": v(-64.31, -46.67) * mm, "end": v(-63.55, -47.7) * mm});
            skLineSegment(sketch, "E1102", {"start": v(-63.55, -47.7) * mm, "end": v(-64.15, -48.15) * mm});
            skLineSegment(sketch, "E1103", {"start": v(-64.15, -48.15) * mm, "end": v(-64.06, -48.27) * mm});
            skLineSegment(sketch, "E1104", {"start": v(-64.06, -48.27) * mm, "end": v(-63.73, -48.71) * mm});
            skLineSegment(sketch, "E1105", {"start": v(-63.73, -48.71) * mm, "end": v(-63.13, -48.26) * mm});
            skLineSegment(sketch, "E1106", {"start": v(-63.13, -48.26) * mm, "end": v(-62.62, -48.92) * mm});
            skLineSegment(sketch, "E1107", {"start": v(-62.62, -48.92) * mm, "end": v(-62.34, -49.27) * mm});
            skLineSegment(sketch, "E1108", {"start": v(-62.34, -49.27) * mm, "end": v(-62.93, -49.74) * mm});
            skLineSegment(sketch, "E1109", {"start": v(-62.93, -49.74) * mm, "end": v(-62.5, -50.28) * mm});
            skLineSegment(sketch, "E1110", {"start": v(-62.5, -50.28) * mm, "end": v(-61.9, -49.82) * mm});
            skLineSegment(sketch, "E1111", {"start": v(-61.9, -49.82) * mm, "end": v(-61.76, -50) * mm});
            skLineSegment(sketch, "E1112", {"start": v(-61.76, -50) * mm, "end": v(-61.1, -50.8) * mm});
            skLineSegment(sketch, "E1113", {"start": v(-61.1, -50.8) * mm, "end": v(-61.67, -51.3) * mm});
            skLineSegment(sketch, "E1114", {"start": v(-61.67, -51.3) * mm, "end": v(-61.45, -51.56) * mm});
            skLineSegment(sketch, "E1115", {"start": v(-61.45, -51.56) * mm, "end": v(-61.22, -51.83) * mm});
            skLineSegment(sketch, "E1116", {"start": v(-61.22, -51.83) * mm, "end": v(-60.65, -51.34) * mm});
            skLineSegment(sketch, "E1117", {"start": v(-60.65, -51.34) * mm, "end": v(-59.97, -52.13) * mm});
            skLineSegment(sketch, "E1118", {"start": v(-59.97, -52.13) * mm, "end": v(-59.81, -52.32) * mm});
            skLineSegment(sketch, "E1119", {"start": v(-59.81, -52.32) * mm, "end": v(-60.37, -52.81) * mm});
            skLineSegment(sketch, "E1120", {"start": v(-60.37, -52.81) * mm, "end": v(-59.9, -53.34) * mm});
            skLineSegment(sketch, "E1121", {"start": v(-59.9, -53.34) * mm, "end": v(-59.35, -52.84) * mm});
            skLineSegment(sketch, "E1122", {"start": v(-59.35, -52.84) * mm, "end": v(-59.05, -53.17) * mm});
            skLineSegment(sketch, "E1123", {"start": v(-59.05, -53.17) * mm, "end": v(-58.49, -53.8) * mm});
            skLineSegment(sketch, "E1124", {"start": v(-58.49, -53.8) * mm, "end": v(-59.04, -54.3) * mm});
            skLineSegment(sketch, "E1125", {"start": v(-59.04, -54.3) * mm, "end": v(-58.66, -54.7) * mm});
            skLineSegment(sketch, "E1126", {"start": v(-58.66, -54.7) * mm, "end": v(-58.56, -54.81) * mm});
            skLineSegment(sketch, "E1127", {"start": v(-58.56, -54.81) * mm, "end": v(-58.01, -54.3) * mm});
            skLineSegment(sketch, "E1128", {"start": v(-58.01, -54.3) * mm, "end": v(-57.13, -55.23) * mm});
            skLineSegment(sketch, "E1129", {"start": v(-57.13, -55.23) * mm, "end": v(-57.67, -55.76) * mm});
            skLineSegment(sketch, "E1130", {"start": v(-57.67, -55.76) * mm, "end": v(-57.18, -56.26) * mm});
            skLineSegment(sketch, "E1131", {"start": v(-57.18, -56.26) * mm, "end": v(-56.64, -55.73) * mm});
            skLineSegment(sketch, "E1132", {"start": v(-56.64, -55.73) * mm, "end": v(-56.19, -56.19) * mm});
            skLineSegment(sketch, "E1133", {"start": v(-56.19, -56.19) * mm, "end": v(-55.73, -56.64) * mm});
            skLineSegment(sketch, "E1134", {"start": v(-55.73, -56.64) * mm, "end": v(-56.26, -57.18) * mm});
            skLineSegment(sketch, "E1135", {"start": v(-56.26, -57.18) * mm, "end": v(-55.76, -57.67) * mm});
            skLineSegment(sketch, "E1136", {"start": v(-55.76, -57.67) * mm, "end": v(-55.23, -57.13) * mm});
            skLineSegment(sketch, "E1137", {"start": v(-55.23, -57.13) * mm, "end": v(-54.3, -58.01) * mm});
            skLineSegment(sketch, "E1138", {"start": v(-54.3, -58.01) * mm, "end": v(-54.81, -58.56) * mm});
            skLineSegment(sketch, "E1139", {"start": v(-54.81, -58.56) * mm, "end": v(-54.7, -58.66) * mm});
            skLineSegment(sketch, "E1140", {"start": v(-54.7, -58.66) * mm, "end": v(-54.3, -59.04) * mm});
            skLineSegment(sketch, "E1141", {"start": v(-54.3, -59.04) * mm, "end": v(-53.8, -58.49) * mm});
            skLineSegment(sketch, "E1142", {"start": v(-53.8, -58.49) * mm, "end": v(-53.17, -59.05) * mm});
            skLineSegment(sketch, "E1143", {"start": v(-53.17, -59.05) * mm, "end": v(-52.84, -59.35) * mm});
            skLineSegment(sketch, "E1144", {"start": v(-52.84, -59.35) * mm, "end": v(-53.34, -59.9) * mm});
            skLineSegment(sketch, "E1145", {"start": v(-53.34, -59.9) * mm, "end": v(-52.81, -60.37) * mm});
            skLineSegment(sketch, "E1146", {"start": v(-52.81, -60.37) * mm, "end": v(-52.32, -59.81) * mm});
            skLineSegment(sketch, "E1147", {"start": v(-52.32, -59.81) * mm, "end": v(-52.13, -59.97) * mm});
            skLineSegment(sketch, "E1148", {"start": v(-52.13, -59.97) * mm, "end": v(-51.34, -60.65) * mm});
            skLineSegment(sketch, "E1149", {"start": v(-51.34, -60.65) * mm, "end": v(-51.83, -61.22) * mm});
            skLineSegment(sketch, "E1150", {"start": v(-51.83, -61.22) * mm, "end": v(-51.56, -61.45) * mm});
            skLineSegment(sketch, "E1151", {"start": v(-51.56, -61.45) * mm, "end": v(-51.3, -61.67) * mm});
            skLineSegment(sketch, "E1152", {"start": v(-51.3, -61.67) * mm, "end": v(-50.8, -61.1) * mm});
            skLineSegment(sketch, "E1153", {"start": v(-50.8, -61.1) * mm, "end": v(-50, -61.76) * mm});
            skLineSegment(sketch, "E1154", {"start": v(-50, -61.76) * mm, "end": v(-49.82, -61.9) * mm});
            skLineSegment(sketch, "E1155", {"start": v(-49.82, -61.9) * mm, "end": v(-50.28, -62.5) * mm});
            skLineSegment(sketch, "E1156", {"start": v(-50.28, -62.5) * mm, "end": v(-49.74, -62.93) * mm});
            skLineSegment(sketch, "E1157", {"start": v(-49.74, -62.93) * mm, "end": v(-49.27, -62.34) * mm});
            skLineSegment(sketch, "E1158", {"start": v(-49.27, -62.34) * mm, "end": v(-48.92, -62.62) * mm});
            skLineSegment(sketch, "E1159", {"start": v(-48.92, -62.62) * mm, "end": v(-48.26, -63.13) * mm});
            skLineSegment(sketch, "E1160", {"start": v(-48.26, -63.13) * mm, "end": v(-48.71, -63.73) * mm});
            skLineSegment(sketch, "E1161", {"start": v(-48.71, -63.73) * mm, "end": v(-48.27, -64.06) * mm});
            skLineSegment(sketch, "E1162", {"start": v(-48.27, -64.06) * mm, "end": v(-48.15, -64.15) * mm});
            skLineSegment(sketch, "E1163", {"start": v(-48.15, -64.15) * mm, "end": v(-47.7, -63.55) * mm});
            skLineSegment(sketch, "E1164", {"start": v(-47.7, -63.55) * mm, "end": v(-46.67, -64.31) * mm});
            skLineSegment(sketch, "E1165", {"start": v(-46.67, -64.31) * mm, "end": v(-47.1, -64.92) * mm});
            skLineSegment(sketch, "E1166", {"start": v(-47.1, -64.92) * mm, "end": v(-46.54, -65.33) * mm});
            skLineSegment(sketch, "E1167", {"start": v(-46.54, -65.33) * mm, "end": v(-46.1, -64.72) * mm});
            skLineSegment(sketch, "E1168", {"start": v(-46.1, -64.72) * mm, "end": v(-45.58, -65.1) * mm});
            skLineSegment(sketch, "E1169", {"start": v(-45.58, -65.1) * mm, "end": v(-45.05, -65.46) * mm});
            skLineSegment(sketch, "E1170", {"start": v(-45.05, -65.46) * mm, "end": v(-45.47, -66.08) * mm});
            skLineSegment(sketch, "E1171", {"start": v(-45.47, -66.08) * mm, "end": v(-44.9, -66.47) * mm});
            skLineSegment(sketch, "E1172", {"start": v(-44.9, -66.47) * mm, "end": v(-44.47, -65.85) * mm});
            skLineSegment(sketch, "E1173", {"start": v(-44.47, -65.85) * mm, "end": v(-43.4, -66.56) * mm});
            skLineSegment(sketch, "E1174", {"start": v(-43.4, -66.56) * mm, "end": v(-43.81, -67.2) * mm});
            skLineSegment(sketch, "E1175", {"start": v(-43.81, -67.2) * mm, "end": v(-43.69, -67.27) * mm});
            skLineSegment(sketch, "E1176", {"start": v(-43.69, -67.27) * mm, "end": v(-43.22, -67.57) * mm});
            skLineSegment(sketch, "E1177", {"start": v(-43.22, -67.57) * mm, "end": v(-42.82, -66.94) * mm});
            skLineSegment(sketch, "E1178", {"start": v(-42.82, -66.94) * mm, "end": v(-42.1, -67.39) * mm});
            skLineSegment(sketch, "E1179", {"start": v(-42.1, -67.39) * mm, "end": v(-41.73, -67.62) * mm});
            skLineSegment(sketch, "E1180", {"start": v(-41.73, -67.62) * mm, "end": v(-42.12, -68.26) * mm});
            skLineSegment(sketch, "E1181", {"start": v(-42.12, -68.26) * mm, "end": v(-41.53, -68.63) * mm});
            skLineSegment(sketch, "E1182", {"start": v(-41.53, -68.63) * mm, "end": v(-41.14, -67.99) * mm});
            skLineSegment(sketch, "E1183", {"start": v(-41.14, -67.99) * mm, "end": v(-40.93, -68.11) * mm});
            skLineSegment(sketch, "E1184", {"start": v(-40.93, -68.11) * mm, "end": v(-40.03, -68.64) * mm});
            skLineSegment(sketch, "E1185", {"start": v(-40.03, -68.64) * mm, "end": v(-40.4, -69.29) * mm});
            skLineSegment(sketch, "E1186", {"start": v(-40.4, -69.29) * mm, "end": v(-40.1, -69.47) * mm});
            skLineSegment(sketch, "E1187", {"start": v(-40.1, -69.47) * mm, "end": v(-39.8, -69.64) * mm});
            skLineSegment(sketch, "E1188", {"start": v(-39.8, -69.64) * mm, "end": v(-39.43, -69) * mm});
            skLineSegment(sketch, "E1189", {"start": v(-39.43, -69) * mm, "end": v(-38.52, -69.5) * mm});
            skLineSegment(sketch, "E1190", {"start": v(-38.52, -69.5) * mm, "end": v(-38.31, -69.62) * mm});
            skLineSegment(sketch, "E1191", {"start": v(-38.31, -69.62) * mm, "end": v(-38.67, -70.28) * mm});
            skLineSegment(sketch, "E1192", {"start": v(-38.67, -70.28) * mm, "end": v(-38.05, -70.61) * mm});
            skLineSegment(sketch, "E1193", {"start": v(-38.05, -70.61) * mm, "end": v(-37.7, -69.95) * mm});
            skLineSegment(sketch, "E1194", {"start": v(-37.7, -69.95) * mm, "end": v(-37.3, -70.16) * mm});
            skLineSegment(sketch, "E1195", {"start": v(-37.3, -70.16) * mm, "end": v(-36.56, -70.55) * mm});
            skLineSegment(sketch, "E1196", {"start": v(-36.56, -70.55) * mm, "end": v(-36.9, -71.22) * mm});
            skLineSegment(sketch, "E1197", {"start": v(-36.9, -71.22) * mm, "end": v(-36.42, -71.47) * mm});
            skLineSegment(sketch, "E1198", {"start": v(-36.42, -71.47) * mm, "end": v(-36.28, -71.54) * mm});
            skLineSegment(sketch, "E1199", {"start": v(-36.28, -71.54) * mm, "end": v(-35.94, -70.87) * mm});
            skLineSegment(sketch, "E1200", {"start": v(-35.94, -70.87) * mm, "end": v(-34.8, -71.44) * mm});
            skLineSegment(sketch, "E1201", {"start": v(-34.8, -71.44) * mm, "end": v(-35.12, -72.12) * mm});
            skLineSegment(sketch, "E1202", {"start": v(-35.12, -72.12) * mm, "end": v(-34.49, -72.42) * mm});
            skLineSegment(sketch, "E1203", {"start": v(-34.49, -72.42) * mm, "end": v(-34.16, -71.74) * mm});
            skLineSegment(sketch, "E1204", {"start": v(-34.16, -71.74) * mm, "end": v(-33.58, -72.02) * mm});
            skLineSegment(sketch, "E1205", {"start": v(-33.58, -72.02) * mm, "end": v(-33, -72.28) * mm});
            skLineSegment(sketch, "E1206", {"start": v(-33, -72.28) * mm, "end": v(-33.3, -72.97) * mm});
            skLineSegment(sketch, "E1207", {"start": v(-33.3, -72.97) * mm, "end": v(-32.67, -73.26) * mm});
            skLineSegment(sketch, "E1208", {"start": v(-32.67, -73.26) * mm, "end": v(-32.36, -72.57) * mm});
            skLineSegment(sketch, "E1209", {"start": v(-32.36, -72.57) * mm, "end": v(-31.19, -73.09) * mm});
            skLineSegment(sketch, "E1210", {"start": v(-31.19, -73.09) * mm, "end": v(-31.48, -73.78) * mm});
            skLineSegment(sketch, "E1211", {"start": v(-31.48, -73.78) * mm, "end": v(-31.34, -73.84) * mm});
            skLineSegment(sketch, "E1212", {"start": v(-31.34, -73.84) * mm, "end": v(-30.83, -74.05) * mm});
            skLineSegment(sketch, "E1213", {"start": v(-30.83, -74.05) * mm, "end": v(-30.54, -73.36) * mm});
            skLineSegment(sketch, "E1214", {"start": v(-30.54, -73.36) * mm, "end": v(-29.77, -73.68) * mm});
            skLineSegment(sketch, "E1215", {"start": v(-29.77, -73.68) * mm, "end": v(-29.36, -73.84) * mm});
            skLineSegment(sketch, "E1216", {"start": v(-29.36, -73.84) * mm, "end": v(-29.63, -74.54) * mm});
            skLineSegment(sketch, "E1217", {"start": v(-29.63, -74.54) * mm, "end": v(-28.98, -74.8) * mm});
            skLineSegment(sketch, "E1218", {"start": v(-28.98, -74.8) * mm, "end": v(-28.7, -74.1) * mm});
            skLineSegment(sketch, "E1219", {"start": v(-28.7, -74.1) * mm, "end": v(-28.48, -74.19) * mm});
            skLineSegment(sketch, "E1220", {"start": v(-28.48, -74.19) * mm, "end": v(-27.5, -74.55) * mm});
            skLineSegment(sketch, "E1221", {"start": v(-27.5, -74.55) * mm, "end": v(-27.76, -75.25) * mm});
            skLineSegment(sketch, "E1222", {"start": v(-27.76, -75.25) * mm, "end": v(-27.43, -75.38) * mm});
            skLineSegment(sketch, "E1223", {"start": v(-27.43, -75.38) * mm, "end": v(-27.1, -75.5) * mm});
            skLineSegment(sketch, "E1224", {"start": v(-27.1, -75.5) * mm, "end": v(-26.85, -74.79) * mm});
            skLineSegment(sketch, "E1225", {"start": v(-26.85, -74.79) * mm, "end": v(-25.87, -75.13) * mm});
            skLineSegment(sketch, "E1226", {"start": v(-25.87, -75.13) * mm, "end": v(-25.64, -75.21) * mm});
            skLineSegment(sketch, "E1227", {"start": v(-25.64, -75.21) * mm, "end": v(-25.88, -75.92) * mm});
            skLineSegment(sketch, "E1228", {"start": v(-25.88, -75.92) * mm, "end": v(-25.21, -76.15) * mm});
            skLineSegment(sketch, "E1229", {"start": v(-25.21, -76.15) * mm, "end": v(-24.98, -75.43) * mm});
            skLineSegment(sketch, "E1230", {"start": v(-24.98, -75.43) * mm, "end": v(-24.56, -75.57) * mm});
            skLineSegment(sketch, "E1231", {"start": v(-24.56, -75.57) * mm, "end": v(-23.76, -75.83) * mm});
            skLineSegment(sketch, "E1232", {"start": v(-23.76, -75.83) * mm, "end": v(-23.98, -76.54) * mm});
            skLineSegment(sketch, "E1233", {"start": v(-23.98, -76.54) * mm, "end": v(-23.45, -76.7) * mm});
            skLineSegment(sketch, "E1234", {"start": v(-23.45, -76.7) * mm, "end": v(-23.3, -76.75) * mm});
            skLineSegment(sketch, "E1235", {"start": v(-23.3, -76.75) * mm, "end": v(-23.09, -76.03) * mm});
            skLineSegment(sketch, "E1236", {"start": v(-23.09, -76.03) * mm, "end": v(-21.86, -76.4) * mm});
            skLineSegment(sketch, "E1237", {"start": v(-21.86, -76.4) * mm, "end": v(-22.06, -77.12) * mm});
            skLineSegment(sketch, "E1238", {"start": v(-22.06, -77.12) * mm, "end": v(-21.39, -77.3) * mm});
            skLineSegment(sketch, "E1239", {"start": v(-21.39, -77.3) * mm, "end": v(-21.18, -76.59) * mm});
            skLineSegment(sketch, "E1240", {"start": v(-21.18, -76.59) * mm, "end": v(-20.57, -76.76) * mm});
            skLineSegment(sketch, "E1241", {"start": v(-20.57, -76.76) * mm, "end": v(-19.95, -76.92) * mm});
            skLineSegment(sketch, "E1242", {"start": v(-19.95, -76.92) * mm, "end": v(-20.13, -77.64) * mm});
            skLineSegment(sketch, "E1243", {"start": v(-20.13, -77.64) * mm, "end": v(-19.45, -77.82) * mm});
            skLineSegment(sketch, "E1244", {"start": v(-19.45, -77.82) * mm, "end": v(-19.27, -77.1) * mm});
            skLineSegment(sketch, "E1245", {"start": v(-19.27, -77.1) * mm, "end": v(-18.02, -77.4) * mm});
            skLineSegment(sketch, "E1246", {"start": v(-18.02, -77.4) * mm, "end": v(-18.2, -78.12) * mm});
            skLineSegment(sketch, "E1247", {"start": v(-18.2, -78.12) * mm, "end": v(-18.04, -78.16) * mm});
            skLineSegment(sketch, "E1248", {"start": v(-18.04, -78.16) * mm, "end": v(-17.5, -78.28) * mm});
            skLineSegment(sketch, "E1249", {"start": v(-17.5, -78.28) * mm, "end": v(-17.34, -77.55) * mm});
            skLineSegment(sketch, "E1250", {"start": v(-17.34, -77.55) * mm, "end": v(-16.52, -77.73) * mm});
            skLineSegment(sketch, "E1251", {"start": v(-16.52, -77.73) * mm, "end": v(-16.09, -77.82) * mm});
            skLineSegment(sketch, "E1252", {"start": v(-16.09, -77.82) * mm, "end": v(-16.24, -78.55) * mm});
            skLineSegment(sketch, "E1253", {"start": v(-16.24, -78.55) * mm, "end": v(-15.55, -78.7) * mm});
            skLineSegment(sketch, "E1254", {"start": v(-15.55, -78.7) * mm, "end": v(-15.4, -77.96) * mm});
            skLineSegment(sketch, "E1255", {"start": v(-15.4, -77.96) * mm, "end": v(-15.16, -78) * mm});
            skLineSegment(sketch, "E1256", {"start": v(-15.16, -78) * mm, "end": v(-14.14, -78.2) * mm});
            skLineSegment(sketch, "E1257", {"start": v(-14.14, -78.2) * mm, "end": v(-14.27, -78.93) * mm});
            skLineSegment(sketch, "E1258", {"start": v(-14.27, -78.93) * mm, "end": v(-13.93, -79) * mm});
            skLineSegment(sketch, "E1259", {"start": v(-13.93, -79) * mm, "end": v(-13.58, -79.05) * mm});
            skLineSegment(sketch, "E1260", {"start": v(-13.58, -79.05) * mm, "end": v(-13.45, -78.31) * mm});
            skLineSegment(sketch, "E1261", {"start": v(-13.45, -78.31) * mm, "end": v(-12.43, -78.49) * mm});
            skLineSegment(sketch, "E1262", {"start": v(-12.43, -78.49) * mm, "end": v(-12.19, -78.52) * mm});
            skLineSegment(sketch, "E1263", {"start": v(-12.19, -78.52) * mm, "end": v(-12.3, -79.26) * mm});
            skLineSegment(sketch, "E1264", {"start": v(-12.3, -79.26) * mm, "end": v(-11.6, -79.37) * mm});
            skLineSegment(sketch, "E1265", {"start": v(-11.6, -79.37) * mm, "end": v(-11.5, -78.63) * mm});
            skLineSegment(sketch, "E1266", {"start": v(-11.5, -78.63) * mm, "end": v(-11.06, -78.7) * mm});
            skLineSegment(sketch, "E1267", {"start": v(-11.06, -78.7) * mm, "end": v(-10.23, -78.8) * mm});
            skLineSegment(sketch, "E1268", {"start": v(-10.23, -78.8) * mm, "end": v(-10.32, -79.54) * mm});
            skLineSegment(sketch, "E1269", {"start": v(-10.32, -79.54) * mm, "end": v(-9.78, -79.62) * mm});
            skLineSegment(sketch, "E1270", {"start": v(-9.78, -79.62) * mm, "end": v(-9.63, -79.63) * mm});
            skLineSegment(sketch, "E1271", {"start": v(-9.63, -79.63) * mm, "end": v(-9.53, -78.89) * mm});
            skLineSegment(sketch, "E1272", {"start": v(-9.53, -78.89) * mm, "end": v(-8.26, -79.03) * mm});
            skLineSegment(sketch, "E1273", {"start": v(-8.26, -79.03) * mm, "end": v(-8.33, -79.78) * mm});
            skLineSegment(sketch, "E1274", {"start": v(-8.33, -79.78) * mm, "end": v(-7.64, -79.85) * mm});
            skLineSegment(sketch, "E1275", {"start": v(-7.64, -79.85) * mm, "end": v(-7.56, -79.1) * mm});
            skLineSegment(sketch, "E1276", {"start": v(-7.56, -79.1) * mm, "end": v(-6.93, -79.16) * mm});
            skLineSegment(sketch, "E1277", {"start": v(-6.93, -79.16) * mm, "end": v(-6.29, -79.21) * mm});
            skLineSegment(sketch, "E1278", {"start": v(-6.29, -79.21) * mm, "end": v(-6.34, -79.96) * mm});
            skLineSegment(sketch, "E1279", {"start": v(-6.34, -79.96) * mm, "end": v(-5.65, -80.01) * mm});
            skLineSegment(sketch, "E1280", {"start": v(-5.65, -80.01) * mm, "end": v(-5.59, -79.27) * mm});
            skLineSegment(sketch, "E1281", {"start": v(-5.59, -79.27) * mm, "end": v(-4.31, -79.35) * mm});
            skLineSegment(sketch, "E1282", {"start": v(-4.31, -79.35) * mm, "end": v(-4.35, -80.1) * mm});
            skLineSegment(sketch, "E1283", {"start": v(-4.35, -80.1) * mm, "end": v(-4.2, -80.1) * mm});
            skLineSegment(sketch, "E1284", {"start": v(-4.2, -80.1) * mm, "end": v(-3.65, -80.13) * mm});
            skLineSegment(sketch, "E1285", {"start": v(-3.65, -80.13) * mm, "end": v(-3.61, -79.38) * mm});
            skLineSegment(sketch, "E1286", {"start": v(-3.61, -79.38) * mm, "end": v(-2.77, -79.42) * mm});
            skLineSegment(sketch, "E1287", {"start": v(-2.77, -79.42) * mm, "end": v(-2.33, -79.43) * mm});
            skLineSegment(sketch, "E1288", {"start": v(-2.33, -79.43) * mm, "end": v(-2.35, -80.18) * mm});
            skLineSegment(sketch, "E1289", {"start": v(-2.35, -80.18) * mm, "end": v(-1.65, -80.2) * mm});
            skLineSegment(sketch, "E1290", {"start": v(-1.65, -80.2) * mm, "end": v(-1.63, -79.45) * mm});
            skLineSegment(sketch, "E1291", {"start": v(-1.63, -79.45) * mm, "end": v(-1.39, -79.45) * mm});
            skLineSegment(sketch, "E1292", {"start": v(-1.39, -79.45) * mm, "end": v(-0.35, -79.46) * mm});
            skLineSegment(sketch, "E1293", {"start": v(-0.35, -79.46) * mm, "end": v(-0.35, -80.21) * mm});
            skLineSegment(sketch, "E1294", {"start": v(-0.35, -80.21) * mm, "end": v(0, -80.21) * mm});
            skLineSegment(sketch, "E1295", {"start": v(0, -80.21) * mm, "end": v(0.35, -80.21) * mm});
            skSolve(sketch);
        }
        {
            var Q0;
            Q0=makeQuery(id+"F0.imprint","IMPRINT",FACE,{"disambiguationData":[TD([[makeQuery(id+"F0.imprint","IMPRINT",EDGE,{"derivedFrom":sQuery(id+"F0.wireOp",EDGE,"E0")}),1.0]])]});
            extrude(context, id + "F1", {"entities" : qUnion([Q0]), "depth" : 6 * mm});
        }
    });
